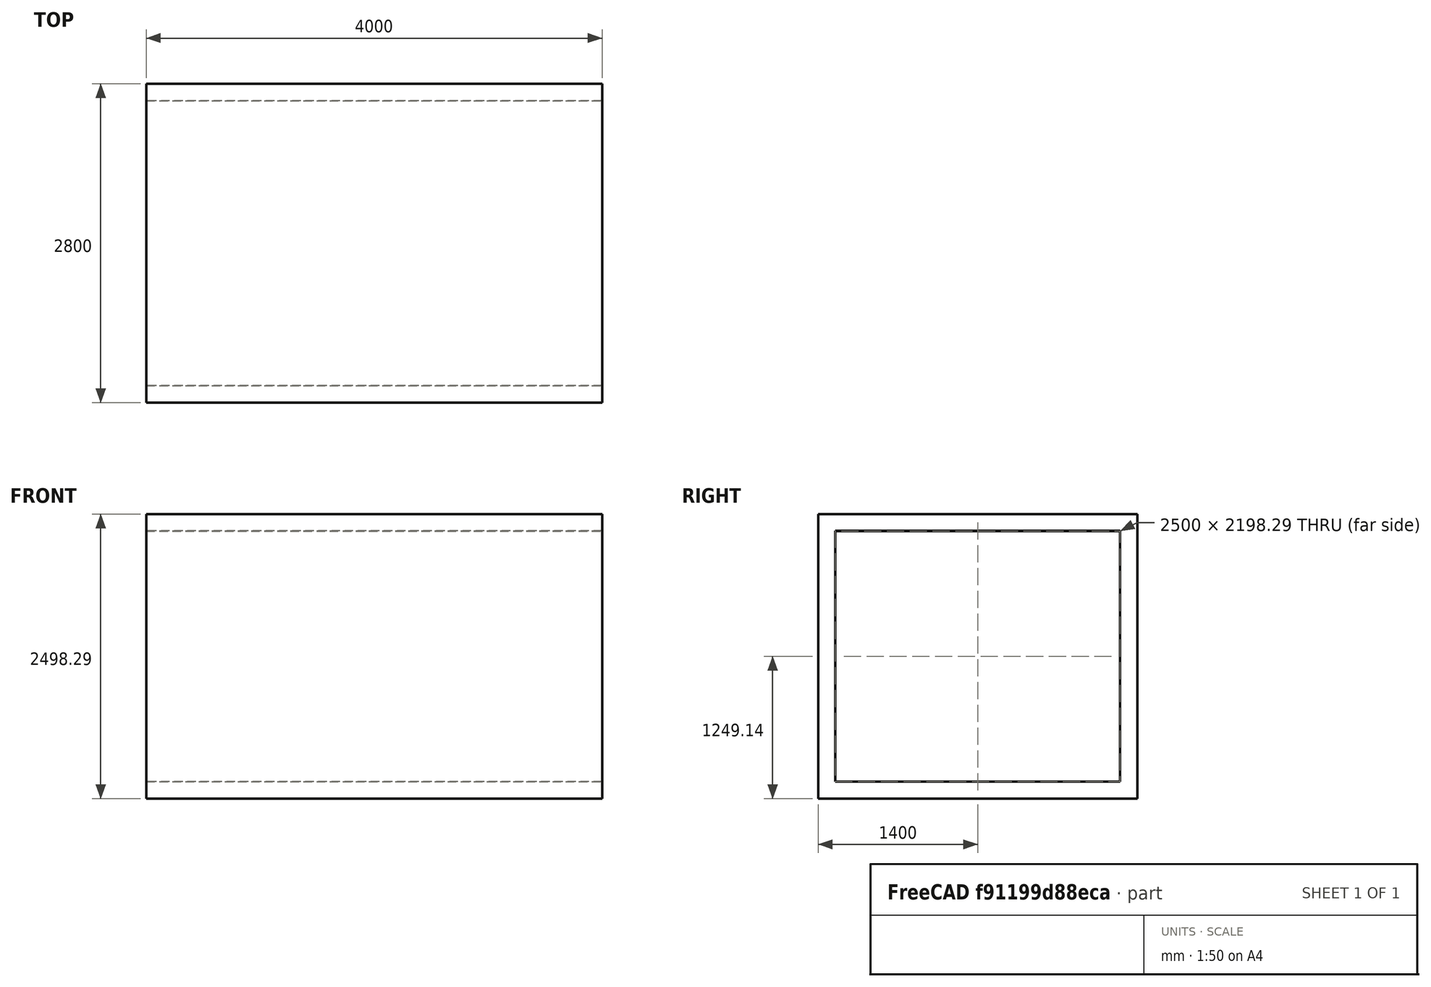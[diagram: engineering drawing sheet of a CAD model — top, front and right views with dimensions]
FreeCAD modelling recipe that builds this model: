
FCSTD DOCUMENT  (FreeCAD 0.17R10276 (Git))
Label: Base Quick Fit Plans 01
License: All rights reserved
LicenseURL: http://en.wikipedia.org/wiki/All_rights_reserved
objects: Part::Feature×204, Part::Part2DObjectPython×170, Part::Mirroring×20, App::DocumentObjectGroup×13, Part::Compound×9, App::FeaturePython×6, App::Annotation×2, Part::Extrusion×2, Part::FeaturePython×2, Part::Thickness×1, Sketcher::SketchObject×1
note: 409 computed .brp shape members not serialized (recipe doc carries the construction recipe); baked Part::Feature solids carry a one-line shape summary decoded from their .brp

FEATURE [Part::Part2DObjectPython] Rectangle  # Draft 2D object (typed FeaturePython)
  ChamferSize = 0
  Columns = 1
  FilletRadius = 0
  Height = 7500
  Length = 6000
  MakeFace = false
  MapMode = -1
  Placement = pos=(-92,-160,0) rot=(0,0,1;0rad)
  Rows = 1
FEATURE [App::FeaturePython] Dimension  # Draft dimension (typed FeaturePython)
  Diameter = false
  Dimline = (6612,4842,0)
  Direction = (0,0,0)
  Distance = 7500
  End = (5908,7340,0)
  LinkedGeometry = -> [Rectangle]
  Normal = (0,0,1)
  Start = (5908,-160,0)
  Support = -> Rectangle
FEATURE [App::FeaturePython] Dimension001  # Draft dimension (typed FeaturePython)
  Diameter = false
  Dimline = (3172,-852,0)
  Direction = (0,0,0)
  Distance = 6000
  End = (5908,-160,0)
  LinkedGeometry = -> [Rectangle]
  Normal = (0,0,1)
  Start = (-92,-160,0)
  Support = -> Rectangle
FEATURE [Part::Part2DObjectPython] Rectangle001  # Draft 2D object (typed FeaturePython)
  ChamferSize = 0
  Columns = 1
  FilletRadius = 0
  Height = 9000
  Length = 5000
  MakeFace = false
  MapMode = -1
  Placement = pos=(9194.87,-160,0) rot=(0,0,1;0rad)
  Rows = 1
FEATURE [App::FeaturePython] Dimension002  # Draft dimension (typed FeaturePython)
  Diameter = false
  Dimline = (15053,4856,0)
  Direction = (0,0,0)
  Distance = 9000
  End = (14194.9,8840,0)
  LinkedGeometry = -> [Rectangle001]
  Normal = (0,0,1)
  Start = (14194.9,-160,0)
  Support = -> Rectangle001
FEATURE [App::FeaturePython] Dimension003  # Draft dimension (typed FeaturePython)
  Diameter = false
  Dimline = (12458.9,-852,0)
  Direction = (0,0,0)
  Distance = 5000
  End = (14194.9,-160,0)
  LinkedGeometry = -> [Rectangle001]
  Normal = (0,0,1)
  Start = (9194.87,-160,0)
  Support = -> Rectangle001
FEATURE [Part::Part2DObjectPython] Rectangle002  # Draft 2D object (typed FeaturePython)
  ChamferSize = 0
  Columns = 1
  FilletRadius = 0
  Height = 11250
  Length = 4000
  MakeFace = false
  MapMode = -1
  Placement = pos=(17670.3,-160,0) rot=(0,0,1;0rad)
  Rows = 1
FEATURE [App::FeaturePython] Dimension004  # Draft dimension (typed FeaturePython)
  Diameter = false
  Dimline = (22786,4857,0)
  Direction = (0,0,0)
  Distance = 11250
  End = (21670.3,11090,0)
  LinkedGeometry = -> [Rectangle002]
  Normal = (0,0,1)
  Start = (21670.3,-160,0)
  Support = -> Rectangle002
FEATURE [App::FeaturePython] Dimension005  # Draft dimension (typed FeaturePython)
  Diameter = false
  Dimline = (20934.3,-852,0)
  Direction = (0,0,0)
  Distance = 4000
  End = (21670.3,-160,0)
  LinkedGeometry = -> [Rectangle002]
  Normal = (0,0,1)
  Start = (17670.3,-160,0)
  Support = -> Rectangle002
FEATURE [Part::Part2DObjectPython] Rectangle011  # Draft 2D object (typed FeaturePython)
  ChamferSize = 0
  Columns = 1
  FilletRadius = 0
  Height = 18
  Length = 900
  MakeFace = true
  Placement = pos=(3354.54,473.858,0) rot=(0.707107,0.707107,0;3.14159rad)
  Rows = 1
FEATURE [Part::Part2DObjectPython] Arc001  # Draft 2D object (typed FeaturePython)
  FirstAngle = -90
  LastAngle = 0
  MakeFace = true
  Placement = pos=(3372.54,473.858,0) rot=(0.707107,0.707107,0;3.14159rad)
  Radius = 900
FEATURE [Part::Part2DObjectPython] Rectangle012  # Draft 2D object (typed FeaturePython)
  ChamferSize = 0
  Columns = 1
  FilletRadius = 0
  Height = 18
  Length = 100
  MakeFace = true
  Placement = pos=(3390.54,373.858,0) rot=(0.707107,0.707107,0;3.14159rad)
  Rows = 1
FEATURE [Part::Part2DObjectPython] Rectangle013  # Draft 2D object (typed FeaturePython)
  ChamferSize = 0
  Columns = 1
  FilletRadius = 0
  Height = 18
  Length = 100
  MakeFace = true
  Placement = pos=(3372.54,373.858,0) rot=(0.707107,0.707107,0;3.14159rad)
  Rows = 1
FEATURE [Part::Part2DObjectPython] Rectangle014  # Draft 2D object (typed FeaturePython)
  ChamferSize = 0
  Columns = 1
  FilletRadius = 0
  Height = 18
  Length = 100
  MakeFace = true
  Placement = pos=(2436.54,373.858,0) rot=(0.707107,0.707107,0;3.14159rad)
  Rows = 1
FEATURE [Part::Part2DObjectPython] Rectangle015  # Draft 2D object (typed FeaturePython)
  ChamferSize = 0
  Columns = 1
  FilletRadius = 0
  Height = 18
  Length = 100
  MakeFace = true
  Placement = pos=(2454.54,373.858,0) rot=(0.707107,0.707107,0;3.14159rad)
  Rows = 1
FEATURE [Part::Compound] Compound001  label="Door-90cm"
  Links = -> [Rectangle015,Rectangle014,Rectangle011,Rectangle012,Arc001,Rectangle013]
  Placement = pos=(12065.1,-4816.3,0) rot=(0,0,1;0rad)
FEATURE [Part::Part2DObjectPython] Rectangle016  # Draft 2D object (typed FeaturePython)
  ChamferSize = 0
  Columns = 1
  FilletRadius = 0
  Height = 1450
  Length = 2250
  MakeFace = false
  Placement = pos=(19234,-3969.83,0) rot=(0.707107,0.707107,0;3.14159rad)
  Rows = 1
FEATURE [Part::Part2DObjectPython] Rectangle017  # Draft 2D object (typed FeaturePython)
  ChamferSize = 0
  Columns = 1
  FilletRadius = 0
  Height = 18
  Length = 800
  MakeFace = true
  Placement = pos=(4414.52,473.858,0) rot=(0.707107,0.707107,0;3.14159rad)
  Rows = 1
FEATURE [Part::Part2DObjectPython] Rectangle018  # Draft 2D object (typed FeaturePython)
  ChamferSize = 0
  Columns = 1
  FilletRadius = 0
  Height = 18
  Length = 100
  MakeFace = true
  Placement = pos=(4450.52,373.858,0) rot=(0.707107,0.707107,0;3.14159rad)
  Rows = 1
FEATURE [Part::Part2DObjectPython] Rectangle019  # Draft 2D object (typed FeaturePython)
  ChamferSize = 0
  Columns = 1
  FilletRadius = 0
  Height = 18
  Length = 100
  MakeFace = true
  Placement = pos=(4432.52,373.858,0) rot=(0.707107,0.707107,0;3.14159rad)
  Rows = 1
FEATURE [Part::Part2DObjectPython] Rectangle020  # Draft 2D object (typed FeaturePython)
  ChamferSize = 0
  Columns = 1
  FilletRadius = 0
  Height = 18
  Length = 100
  MakeFace = true
  Placement = pos=(3596.52,373.858,0) rot=(0.707107,0.707107,0;3.14159rad)
  Rows = 1
FEATURE [Part::Part2DObjectPython] Rectangle021  # Draft 2D object (typed FeaturePython)
  ChamferSize = 0
  Columns = 1
  FilletRadius = 0
  Height = 18
  Length = 100
  MakeFace = true
  Placement = pos=(3614.52,373.858,0) rot=(0.707107,0.707107,0;3.14159rad)
  Rows = 1
FEATURE [Part::Part2DObjectPython] Rectangle022  # Draft 2D object (typed FeaturePython)
  ChamferSize = 0
  Columns = 1
  FilletRadius = 0
  Height = 1655.27
  Length = 2455.27
  MakeFace = false
  Placement = pos=(19131.4,-4072.46,0) rot=(0.707107,0.707107,0;3.14159rad)
  Rows = 1
FEATURE [Part::Part2DObjectPython] Rectangle023  # Draft 2D object (typed FeaturePython)
  ChamferSize = 0
  Columns = 1
  FilletRadius = 0
  Height = 800
  Length = 800
  MakeFace = true
  Placement = pos=(21405.4,-1242.94,0) rot=(0.707107,0.707107,0;3.14159rad)
  Rows = 1
FEATURE [Part::Part2DObjectPython] Rectangle024  # Draft 2D object (typed FeaturePython)
  ChamferSize = 0
  Columns = 1
  FilletRadius = 0
  Height = 760
  Length = 760
  MakeFace = true
  Placement = pos=(21425.4,-1222.94,0) rot=(0.707107,0.707107,0;3.14159rad)
  Rows = 1
FEATURE [Part::Feature] Face
  Placement = pos=(15980.4,-1398.57,0) rot=(0,0,1;0rad)
  shape: bbox 800 x 800 x 2e-07 mm, 1 faces, 0 solids (baked)
FEATURE [Part::Part2DObjectPython] Rectangle025  # Draft 2D object (typed FeaturePython)
  ChamferSize = 0
  Columns = 1
  FilletRadius = 0
  Height = 760
  Length = 760
  MakeFace = true
  Placement = pos=(21425.4,-1222.94,0) rot=(0.707107,0.707107,0;3.14159rad)
  Rows = 1
FEATURE [Part::Part2DObjectPython] Line001  # Draft 2D object (typed FeaturePython)
  ChamferSize = 0
  Closed = false
  End = (21425.4,-1222.94,0)
  FilletRadius = 0
  Length = 1074.8
  MakeFace = true
  Placement = pos=(15980.4,-1398.57,0) rot=(0,0,1;0rad)
  Points = (2) [(6204.98,935.631,0),(5444.98,175.631,0)]
  Start = (22185.4,-462.938,0)
  Subdivisions = 0
FEATURE [Part::Part2DObjectPython] Line002  # Draft 2D object (typed FeaturePython)
  ChamferSize = 0
  Closed = false
  End = (22185.4,-1222.94,0)
  FilletRadius = 0
  Length = 1074.8
  MakeFace = true
  Placement = pos=(15980.4,-1398.57,0) rot=(0,0,1;0rad)
  Points = (2) [(5444.98,935.631,0),(6204.98,175.631,0)]
  Start = (21425.4,-462.938,0)
  Subdivisions = 0
FEATURE [Part::Part2DObjectPython] Block  label="Shower"  # Draft 2D object (typed FeaturePython)
  Components = -> [Line002,Line001,Rectangle025,Face]
  Placement = pos=(-1521.4,-1276.89,0) rot=(0,0,1;0rad)
FEATURE [Part::Part2DObjectPython] Rectangle026  # Draft 2D object (typed FeaturePython)
  ChamferSize = 0
  Columns = 1
  FilletRadius = 30
  Height = 370
  Length = 170
  MakeFace = true
  Placement = pos=(22375.3,-1817.54,0) rot=(0.707107,0.707107,0;3.14159rad)
  Rows = 1
FEATURE [Part::Part2DObjectPython] Circle  # Draft 2D object (typed FeaturePython)
  FirstAngle = 0
  LastAngle = 0
  MakeFace = true
  Placement = pos=(22560.3,-1732.54,0) rot=(0.707107,0.707107,0;3.14159rad)
  Radius = 10
  Support = -> [Rectangle026]
FEATURE [Part::Feature] Compound003  label="WC001"
  Placement = pos=(12977.9,-1470.8,0) rot=(0,0,1;0rad)
  shape: bbox 370 x 660 x 2e-07 mm, 2 faces, 0 solids (baked)
FEATURE [Part::Part2DObjectPython] Rectangle027  # Draft 2D object (typed FeaturePython)
  ChamferSize = 0
  Columns = 1
  FilletRadius = 50
  Height = 300
  Length = 500
  MakeFace = true
  Placement = pos=(21444.9,-2450.78,0) rot=(0.707107,0.707107,0;3.14159rad)
  Rows = 1
FEATURE [Part::Part2DObjectPython] Circle001  # Draft 2D object (typed FeaturePython)
  FirstAngle = 0
  LastAngle = 0
  MakeFace = true
  Placement = pos=(5532.19,-802.214,0) rot=(0,0,1;0rad)
  Radius = 12
FEATURE [Part::Feature] Face003
  shape: bbox 278.9 x 478.9 x 2e-07 mm, 1 faces, 0 solids (baked)
FEATURE [Part::Feature] Face004
  Placement = pos=(15980.4,-1398.57,0) rot=(0,0,1;0rad)
  shape: bbox 278.9 x 478.9 x 2e-07 mm, 1 faces, 0 solids (baked)
FEATURE [Part::Feature] Face005
  shape: bbox 300 x 500 x 2e-07 mm, 1 faces, 0 solids (baked)
FEATURE [Part::Compound] Compound004  label="Sink 1"
  Links = -> [Face005,Face003,Circle001]
  Placement = pos=(13769.5,-2367.61,0) rot=(0,0,1;0rad)
FEATURE [Part::Feature] Compound005  label="Sink"
  Placement = pos=(18979.2,3570.08,0) rot=(0,0,-1;1.5708rad)
  shape: bbox 500 x 300 x 2e-07 mm, 3 faces, 0 solids (baked)
FEATURE [Part::Feature] Compound006  label="WC002"
  Placement = pos=(12181.7,-1602.71,0) rot=(0,0,1;0rad)
  shape: bbox 370 x 660 x 2e-07 mm, 2 faces, 0 solids (baked)
FEATURE [Part::Part2DObjectPython] Arc002  # Draft 2D object (typed FeaturePython)
  FirstAngle = -90
  LastAngle = 0
  MakeFace = true
  Placement = pos=(4432.52,473.858,0) rot=(0.707107,0.707107,0;3.14159rad)
  Radius = 800
FEATURE [Part::Compound] Compound007  label="Door-80cm"
  Links = -> [Rectangle019,Rectangle017,Rectangle018,Rectangle020,Rectangle021,Arc002]
  Placement = pos=(12065.1,-4816.3,0) rot=(0,0,1;0rad)
FEATURE [Part::Part2DObjectPython] Rectangle028  # Draft 2D object (typed FeaturePython)
  ChamferSize = 0
  Columns = 1
  FilletRadius = 0
  Height = 400
  Length = 400
  MakeFace = true
  Placement = pos=(17670.3,-160,0) rot=(0.707107,0.707107,0;3.14159rad)
  Rows = 1
  Support = -> [Rectangle002]
FEATURE [Part::Feature] mirror008  label="Mirror of 90cm door001"
  Placement = pos=(3560.22,2517.25,0) rot=(0,0,1;0rad)
  shape: bbox 972 x 1000 x 2e-07 mm, 5 faces, 0 solids (baked)
FEATURE [Part::Feature] Compound010  label="90cm door003"
  Placement = pos=(22653.3,641.465,0) rot=(0,0,1;0rad)
  shape: bbox 972 x 1000 x 2e-07 mm, 5 faces, 0 solids (baked)
FEATURE [Part::Part2DObjectPython] Line003  # Draft 2D object (typed FeaturePython)
  ChamferSize = 0
  Closed = false
  End = (23811.8,1115.32,0)
  FilletRadius = 0
  Length = 1314
  MakeFace = true
  Placement = pos=(4391.51,-222,0) rot=(0,0,1;0rad)
  Points = (2) [(20734.3,1337.32,0),(19420.3,1337.32,0)]
  Start = (25125.8,1115.32,0)
  Subdivisions = 0
FEATURE [Part::Part2DObjectPython] Line  # Draft 2D object (typed FeaturePython)
  ChamferSize = 0
  Closed = false
  End = (26367.1,1115.32,0)
  FilletRadius = 0
  Length = 2499.64
  MakeFace = true
  Placement = pos=(4497.18,0,0) rot=(0,0,1;0rad)
  Points = (2) [(19370.3,1115.32,0),(21870,1115.32,0)]
  Start = (23867.5,1115.32,0)
  Subdivisions = 0
FEATURE [Part::Part2DObjectPython] Line005  # Draft 2D object (typed FeaturePython)
  ChamferSize = 0
  Closed = false
  End = (26261.5,960.561,0)
  FilletRadius = 0
  Length = 2499.64
  MakeFace = true
  Placement = pos=(4391.51,0,0) rot=(0,0,1;0rad)
  Points = (2) [(19370.3,960.561,0),(21870,960.561,0)]
  Start = (23761.8,960.561,0)
  Subdivisions = 0
FEATURE [App::DocumentObjectGroup] Construction
  Group = -> [Compound010,Line003,Line,Line005]
FEATURE [Part::Part2DObjectPython] Rectangle049  # Draft 2D object (typed FeaturePython)
  ChamferSize = 0
  Columns = 1
  FilletRadius = 0
  Height = 1900
  Length = 1400
  MakeFace = true
  Placement = pos=(-5091.08,-778.605,0) rot=(0,0,1;0rad)
  Rows = 1
FEATURE [Part::Part2DObjectPython] Rectangle050  # Draft 2D object (typed FeaturePython)
  ChamferSize = 0
  Columns = 1
  FilletRadius = 0
  Height = 1900
  Length = 910
  MakeFace = true
  Placement = pos=(-6241.3,-778.605,0) rot=(0,0,1;0rad)
  Rows = 1
FEATURE [Part::Part2DObjectPython] Rectangle051  # Draft 2D object (typed FeaturePython)
  ChamferSize = 0
  Columns = 1
  FilletRadius = 0
  Height = 300
  Length = 910
  MakeFace = true
  Placement = pos=(-6241.3,821.395,0) rot=(0,0,1;0rad)
  Rows = 1
FEATURE [Part::Part2DObjectPython] Line008  # Draft 2D object (typed FeaturePython)
  ChamferSize = 0
  Closed = false
  End = (-5786.3,821.395,0)
  FilletRadius = 0
  Length = 647.012
  MakeFace = true
  Points = (2) [(-6241.3,361.395,0),(-5786.3,821.395,0)]
  Start = (-6241.3,361.395,0)
  Subdivisions = 0
FEATURE [Part::Part2DObjectPython] DWire001  # Draft 2D object (typed FeaturePython)
  ChamferSize = 0
  Closed = true
  End = (-6241.3,361.395,0)
  FilletRadius = 0
  Length = 1562.01
  MakeFace = true
  Points = (3) [(-5786.3,821.395,0),(-5786.3,361.395,0),(-6241.3,361.395,0)]
  Start = (-5786.3,821.395,0)
  Subdivisions = 0
FEATURE [Part::Part2DObjectPython] DWire002  # Draft 2D object (typed FeaturePython)
  ChamferSize = 0
  Closed = true
  End = (-5091.08,361.395,0)
  FilletRadius = 0
  Length = 1562.01
  MakeFace = true
  Placement = pos=(1150.22,0,0) rot=(0,0,1;0rad)
  Points = (3) [(-5786.3,821.395,0),(-5786.3,361.395,0),(-6241.3,361.395,0)]
  Start = (-4636.08,821.395,0)
  Subdivisions = 0
FEATURE [Part::Part2DObjectPython] Rectangle052  # Draft 2D object (typed FeaturePython)
  ChamferSize = 0
  Columns = 1
  FilletRadius = 0
  Height = 300
  Length = 700
  MakeFace = true
  Placement = pos=(-5091.08,821.395,0) rot=(0,0,1;0rad)
  Rows = 1
FEATURE [Part::Part2DObjectPython] Rectangle053  # Draft 2D object (typed FeaturePython)
  ChamferSize = 0
  Columns = 1
  FilletRadius = 0
  Height = 300
  Length = 700
  MakeFace = true
  Placement = pos=(-4391.08,821.395,0) rot=(0,0,1;0rad)
  Rows = 1
FEATURE [Part::Compound] Compound009  label="Bed-Twin"
  Links = -> [Rectangle050,Rectangle051,Line008,DWire001]
FEATURE [App::DocumentObjectGroup] Group003  label="Assets"
  Group = -> [Compound005,Compound006,Compound001,Compound007,Compound009]
FEATURE [Part::Part2DObjectPython] DWire005  # Draft 2D object (typed FeaturePython)
  ChamferSize = 0
  Closed = true
  End = (-3474.44,-2441.09,0)
  FilletRadius = 0
  Length = 5366.71
  MakeFace = true
  Points = (8) [(-3691.08,-2441.09,0),(-3691.08,-1691.09,0),(-2291.08,-1691.09,0),(-2291.08,-2441.09,0),(-2507.72,-2441.09,0),(-2507.72,-1907.73,0),+2 more]
  Start = (-3691.08,-2441.09,0)
  Subdivisions = 0
FEATURE [Part::Part2DObjectPython] Rectangle035  # Draft 2D object (typed FeaturePython)
  ChamferSize = 0
  Columns = 1
  FilletRadius = 0
  Height = 533.356
  Length = 966.713
  MakeFace = true
  Placement = pos=(-3474.44,-2441.09,0) rot=(0,0,1;0rad)
  Rows = 1
FEATURE [Part::Part2DObjectPython] Line012  # Draft 2D object (typed FeaturePython)
  ChamferSize = 0
  Closed = false
  End = (-2991.08,-2441.09,0)
  FilletRadius = 0
  Length = 533.356
  MakeFace = true
  Points = (2) [(-2991.08,-1907.73,0),(-2991.08,-2441.09,0)]
  Start = (-2991.08,-1907.73,0)
  Subdivisions = 0
FEATURE [Part::Part2DObjectPython] Line004  # Draft 2D object (typed FeaturePython)
  ChamferSize = 0
  Closed = false
  End = (-947.957,-2441.09,0)
  FilletRadius = 0
  Length = 533.356
  MakeFace = true
  Placement = pos=(2043.12,0,0) rot=(0,0,1;0rad)
  Points = (2) [(-2991.08,-1907.73,0),(-2991.08,-2441.09,0)]
  Start = (-947.957,-1907.73,0)
  Subdivisions = 0
FEATURE [Part::Part2DObjectPython] DWire006  # Draft 2D object (typed FeaturePython)
  ChamferSize = 0
  Closed = true
  End = (-1431.31,-2441.09,0)
  FilletRadius = 0
  Length = 6333.43
  MakeFace = true
  Placement = pos=(2043.12,0,0) rot=(0,0,1;0rad)
  Points = (8) [(-3691.08,-2441.09,0),(-3691.08,-1691.09,0),(-1807.72,-1691.09,0),(-1807.72,-2441.09,0),(-2024.37,-2441.09,0),(-2024.37,-1907.73,0),+2 more]
  Start = (-1647.96,-2441.09,0)
  Subdivisions = 0
FEATURE [Part::Part2DObjectPython] DWire007  # Draft 2D object (typed FeaturePython)
  ChamferSize = 0
  Closed = true
  End = (-5457.85,-2441.09,0)
  FilletRadius = 0
  Length = 4400
  MakeFace = true
  Placement = pos=(-1983.42,0,0) rot=(0,0,1;0rad)
  Points = (8) [(-3691.08,-2441.09,0),(-3691.08,-1691.09,0),(-2774.44,-1691.09,0),(-2774.44,-2441.09,0),(-2991.08,-2441.09,0),(-2991.08,-1907.73,0),+2 more]
  Start = (-5674.49,-2441.09,0)
  Subdivisions = 0
FEATURE [Part::Part2DObjectPython] Rectangle037  # Draft 2D object (typed FeaturePython)
  ChamferSize = 0
  Columns = 1
  FilletRadius = 0
  Height = 533.356
  Length = 483.356
  MakeFace = true
  Placement = pos=(-5457.85,-2441.09,0) rot=(0,0,1;0rad)
  Rows = 1
FEATURE [Part::Compound] Compound021  label="Sofa - 1"
  Links = -> [DWire005,Rectangle035,Line012]
FEATURE [Part::Compound] Compound011  label="Sofa - 2"
  Links = -> [Rectangle037,DWire007]
FEATURE [Part::Part2DObjectPython] Rectangle038  # Draft 2D object (typed FeaturePython)
  ChamferSize = 0
  Columns = 1
  FilletRadius = 0
  Height = 533.356
  Length = 1450.07
  MakeFace = true
  Placement = pos=(-1431.31,-2441.09,0) rot=(0,0,1;0rad)
  Rows = 1
FEATURE [Part::Part2DObjectPython] Line006  # Draft 2D object (typed FeaturePython)
  ChamferSize = 0
  Closed = false
  End = (-464.6,-2441.09,0)
  FilletRadius = 0
  Length = 533.356
  MakeFace = true
  Placement = pos=(2526.48,0,0) rot=(0,0,1;0rad)
  Points = (2) [(-2991.08,-1907.73,0),(-2991.08,-2441.09,0)]
  Start = (-464.6,-1907.73,0)
  Subdivisions = 0
FEATURE [Part::Compound] Compound022  label="Sofa - 3"
  Links = -> [Line004,DWire006,Rectangle038,Line006]
FEATURE [Part::Compound] Compound008  label="Bed-Double"
  Links = -> [Rectangle049,DWire002,Rectangle052,Rectangle053]
FEATURE [Part::Feature] Compound024  label="90cm door005"
  Placement = pos=(26285.8,79.011,0) rot=(0,0,1;1.5708rad)
  shape: bbox 1000 x 972 x 2e-07 mm, 5 faces, 0 solids (baked)
FEATURE [Part::Part2DObjectPython] Rectangle054  # Draft 2D object (typed FeaturePython)
  ChamferSize = 0
  Columns = 1
  FilletRadius = 0
  Height = 600
  Length = 2923.45
  MakeFace = true
  Placement = pos=(18270.3,2237.32,0) rot=(0,0,1;1.5708rad)
  Rows = 1
FEATURE [Part::Mirroring] mirror009  label="Mirror of Sink"
  Base = (18377,-1894.45,0)
  Normal = (0,1,0)
  Source = -> Compound005
FEATURE [Part::Feature] mirror010  label="Mirror of Sink001"
  Placement = pos=(19714.8,21927.3,0) rot=(0,0,-1;1.5708rad)
  shape: bbox 300 x 500 x 2e-07 mm, 3 faces, 0 solids (baked)
FEATURE [Part::Feature] Shell002  label="Dinning 002"
  Placement = pos=(-2420.47,1941.18,0) rot=(0,0,1;0rad)
  shape: bbox 2057 x 2057 x 2e-07 mm, 5 faces, 0 solids (baked)
FEATURE [Part::Feature] Shell003  label="Dinning 003"
  Placement = pos=(-7725.86,-2470.88,0) rot=(0,0,1;0rad)
  shape: bbox 2057 x 2057 x 2e-07 mm, 5 faces, 0 solids (baked)
FEATURE [Part::Feature] Compound027  label="dinning001"
  Placement = pos=(-14334.8,-3411.08,0) rot=(0,0,1;0rad)
  shape: bbox 2057 x 1200 x 2e-07 mm, 5 faces, 0 solids (baked)
FEATURE [Part::Feature] Compound029  label="Door-90cm002"
  Placement = pos=(4421.79,-3083.36,0) rot=(0,0,1;0rad)
  shape: bbox 972 x 1000 x 2e-07 mm, 5 faces, 0 solids (baked)
FEATURE [Part::Feature] Compound030  label="Bed-Double003"
  Placement = pos=(9599.08,5590.61,0) rot=(0,0,1;0rad)
  shape: bbox 1400 x 1900 x 2e-07 mm, 4 faces, 0 solids (baked)
FEATURE [Part::Feature] mirror013  label="Mirror of Shower002"
  Placement = pos=(-9357.23,5973.34,0) rot=(0,0,1;0rad)
  shape: bbox 800 x 800 x 2e-07 mm, 2 faces, 0 solids (baked)
FEATURE [Part::Feature] mirror017  label="Mirror of Sofa - 006"
  Placement = pos=(5211.98,2057.23,0) rot=(0,0,1;0rad)
  shape: bbox 1400 x 750 x 2e-07 mm, 2 faces, 0 solids (baked)
FEATURE [Part::Feature] Compound031  label="Sofa - 006"
  Placement = pos=(27672.7,9569.4,0) rot=(0,0,1;0rad)
  shape: bbox 1400 x 750 x 2e-07 mm, 2 faces, 0 solids (baked)
FEATURE [Part::Feature] Compound034  label="Bed-Double004"
  Placement = pos=(15177.5,-4723.55,0) rot=(0,0,1;0rad)
  shape: bbox 1400 x 1900 x 2e-07 mm, 4 faces, 0 solids (baked)
FEATURE [Part::Feature] Compound035  label="Bed-Double005"
  Placement = pos=(12639.4,2140.46,0) rot=(0,0,1;1.5708rad)
  shape: bbox 1900 x 1400 x 2e-07 mm, 4 faces, 0 solids (baked)
FEATURE [Part::Part2DObjectPython] Rectangle070  # Draft 2D object (typed FeaturePython)
  ChamferSize = 0
  Columns = 1
  FilletRadius = 0
  Height = 3000
  Length = 3000
  MakeFace = true
  Placement = pos=(6000,-9774.06,0) rot=(0,0,1;0rad)
  Rows = 1
FEATURE [Part::Part2DObjectPython] Rectangle072  # Draft 2D object (typed FeaturePython)
  ChamferSize = 0
  Columns = 1
  FilletRadius = 0
  Height = 600
  Length = 3599.13
  MakeFace = true
  Placement = pos=(2308.87,8523.32,0) rot=(0,0,1;0rad)
  Rows = 1
FEATURE [Part::Feature] mirror030  label="Mirror of Sink 005"
  Placement = pos=(4044.83,28204.3,0) rot=(0,0,-1;1.5708rad)
  shape: bbox 500 x 300 x 2e-07 mm, 3 faces, 0 solids (baked)
FEATURE [Part::Part2DObjectPython] Rectangle073  # Draft 2D object (typed FeaturePython)
  ChamferSize = 0
  Columns = 1
  FilletRadius = 0
  Height = 1950
  Length = 950
  MakeFace = true
  Placement = pos=(1798.43,-5839.95,0) rot=(0,0,1;0rad)
  Rows = 1
FEATURE [App::DocumentObjectGroup] Group006  label="Plan Layout 2"
  Group = -> [Compound035,Rectangle070,Rectangle073]
FEATURE [App::DocumentObjectGroup] Group001  label="9mx5m"
  Group = -> [Dimension002,Dimension003,Rectangle001,Group006]
FEATURE [Part::Feature] Compound048
  Placement = pos=(2515.93,6885.08,0) rot=(0,0,-1;1.5708rad)
  shape: bbox 1950 x 2057 x 2e-07 mm, 7 faces, 0 solids (baked)
FEATURE [Part::Feature] Compound049
  Placement = pos=(-6428.78,862.396,0) rot=(0,0,1;0rad)
  shape: bbox 2057 x 1950 x 2e-07 mm, 7 faces, 0 solids (baked)
FEATURE [Part::Part2DObjectPython] Line016  # Draft 2D object (typed FeaturePython)
  ChamferSize = 0
  Closed = false
  End = (5908,8823.32,0)
  FilletRadius = 0
  Length = 3599.13
  MakeFace = true
  Placement = pos=(0,1783.32,0) rot=(0,0,1;0rad)
  Points = (2) [(2308.87,7040,0),(5908,7040,0)]
  Start = (2308.87,8823.32,0)
  Subdivisions = 0
FEATURE [Part::Part2DObjectPython] Rectangle075  # Draft 2D object (typed FeaturePython)
  ChamferSize = 0
  Columns = 1
  FilletRadius = 0
  Height = 600
  Length = 150.814
  MakeFace = false
  Placement = pos=(3257.19,2489.19,0) rot=(0,0,1;0rad)
  Rows = 1
FEATURE [Part::Part2DObjectPython] Rectangle078  # Draft 2D object (typed FeaturePython)
  ChamferSize = 0
  Columns = 1
  FilletRadius = 0
  Height = 2500
  Length = 4000
  MakeFace = false
  Placement = pos=(17670.3,8590,0) rot=(0,0,1;0rad)
  Rows = 1
FEATURE [Part::Part2DObjectPython] Rectangle079  # Draft 2D object (typed FeaturePython)
  ChamferSize = 0
  Columns = 1
  FilletRadius = 0
  Height = 7500
  Length = 3752.68
  MakeFace = false
  Placement = pos=(2155.32,-160,0) rot=(0,0,1;0rad)
  Rows = 7
FEATURE [App::Annotation] Text
  LabelText = Single Bed Unit 45 sq m | 1 Bed | Bath | Kitchen | Living
  Position = (-173.725,11590.6,0)
FEATURE [Part::Part2DObjectPython] Line017  # Draft 2D object (typed FeaturePython)
  ChamferSize = 0
  Closed = false
  End = (19420.3,11090,0)
  FilletRadius = 0
  Length = 8852.68
  MakeFace = true
  Points = (2) [(19420.3,2237.32,0),(19420.3,11090,0)]
  Start = (19420.3,2237.32,0)
  Subdivisions = 0
FEATURE [Part::Feature] Compound012  label="Bed-Double002"
  Placement = pos=(18791.7,14231.1,0) rot=(0,0,1;1.5708rad)
  shape: bbox 1900 x 1400 x 2e-07 mm, 4 faces, 0 solids (baked)
FEATURE [App::DocumentObjectGroup] Group005  label="Plan Layout 3"
  Group = -> [Rectangle054,Compound012,mirror017,Compound031,Compound024,mirror010]
FEATURE [App::DocumentObjectGroup] Group002  label="11.5mx4m"
  Group = -> [Dimension004,Dimension005,Rectangle002,Group005]
FEATURE [Part::Feature] Compound  label="Sofa - 007"
  Placement = pos=(19318.3,10129.4,0) rot=(0,0,1;0rad)
  shape: bbox 1883 x 750 x 2e-07 mm, 2 faces, 0 solids (baked)
FEATURE [Part::Part2DObjectPython] Rectangle082  # Draft 2D object (typed FeaturePython)
  ChamferSize = 0
  Columns = 1
  FilletRadius = 0
  Height = 2803.44
  Length = 4303.44
  MakeFace = false
  Placement = pos=(17518.6,8438.28,0) rot=(0,0,1;0rad)
  Rows = 1
FEATURE [App::DocumentObjectGroup] Group007  label="Info"
  Group = -> [Text]
FEATURE [Part::Part2DObjectPython] Rectangle083  # Draft 2D object (typed FeaturePython)
  ChamferSize = 0
  Columns = 1
  FilletRadius = 0
  Height = 950
  Length = 950
  MakeFace = true
  Placement = pos=(18152.7,6324.53,0) rot=(0.707107,0.707107,0;3.14159rad)
  Rows = 1
FEATURE [Part::Feature] mirror035  label="Mirror of Sofa - 016"
  shape: bbox 1883 x 750 x 2e-07 mm, 2 faces, 0 solids (baked)
FEATURE [Part::Part2DObjectPython] Line023  # Draft 2D object (typed FeaturePython)
  ChamferSize = 0
  Closed = false
  End = (21670.3,5160.77,0)
  FilletRadius = 0
  Length = 4000
  MakeFace = true
  Points = (2) [(17670.3,5160.77,0),(21670.3,5160.77,0)]
  Start = (17670.3,5160.77,0)
  Subdivisions = 0
FEATURE [Part::Feature] Compound051  label="dinning003"
  Placement = pos=(29919.6,-14497.4,0) rot=(0,0,1;1.5708rad)
  shape: bbox 1200 x 2057 x 2e-07 mm, 5 faces, 0 solids (baked)
FEATURE [Part::Part2DObjectPython] Rectangle090  # Draft 2D object (typed FeaturePython)
  ChamferSize = 0
  Columns = 1
  FilletRadius = 0
  Height = 3349.19
  Length = 150
  MakeFace = false
  Placement = pos=(-92,1289.19,0) rot=(0,0,-1;1.5708rad)
  Rows = 1
FEATURE [Part::Feature] mirror044  label="Mirror of Mirror of Shower002"
  Placement = pos=(-2698.48,-4e-12,0) rot=(0,0,1;0rad)
  shape: bbox 800 x 800 x 2e-07 mm, 2 faces, 0 solids (baked)
FEATURE [Part::Feature] mirror045  label="Mirror of Mirror of WC003"
  Placement = pos=(-2698.48,-4e-12,0) rot=(0,0,1;0rad)
  shape: bbox 370 x 660 x 2e-07 mm, 2 faces, 0 solids (baked)
FEATURE [Part::Feature] mirror046  label="Mirror of Rectangle090"
  Placement = pos=(-2698.48,-4e-12,0) rot=(0,0,1;0rad)
  shape: bbox 1900 x 2547 x 2e-07 mm, 0 faces, 0 solids (baked)
FEATURE [Part::Feature] mirror047  label="Mirror of Rectangle091"
  Placement = pos=(-2698.48,-4e-12,0) rot=(0,0,1;0rad)
  shape: bbox 1600 x 2247 x 2e-07 mm, 0 faces, 0 solids (baked)
FEATURE [Part::Feature] mirror048  label="Mirror of Mirror of Sink 007"
  Placement = pos=(-2698.48,-4e-12,0) rot=(0,0,1;0rad)
  shape: bbox 300 x 500 x 2e-07 mm, 3 faces, 0 solids (baked)
FEATURE [Part::Part2DObjectPython] Rectangle092  # Draft 2D object (typed FeaturePython)
  ChamferSize = 0
  Columns = 6
  FilletRadius = 0
  Height = 4000
  Length = 6502.68
  MakeFace = false
  Placement = pos=(17670.3,2087.32,0) rot=(0.707107,0.707107,0;3.14159rad)
  Rows = 1
FEATURE [Part::Feature] Compound052  label="Sofa - 008"
  Placement = pos=(1555.96,6630.22,0) rot=(0,0,1;0rad)
  shape: bbox 1883 x 750 x 2e-07 mm, 2 faces, 0 solids (baked)
FEATURE [Part::Part2DObjectPython] Rectangle093  # Draft 2D object (typed FeaturePython)
  ChamferSize = 0
  Columns = 1
  FilletRadius = 0
  Height = 950
  Length = 950
  MakeFace = true
  Placement = pos=(390.401,2825.38,0) rot=(0.707107,0.707107,0;3.14159rad)
  Rows = 1
FEATURE [Part::Feature] mirror052  label="Mirror of Sofa - 017"
  Placement = pos=(-17762.3,-3499.15,0) rot=(0,0,1;0rad)
  shape: bbox 1883 x 750 x 2e-07 mm, 2 faces, 0 solids (baked)
FEATURE [Part::Feature] mirror053  label="Mirror of Bed-Double005"
  Placement = pos=(-2125.14,1590.4,0) rot=(0,0,1;0rad)
  shape: bbox 1400 x 1900 x 2e-07 mm, 4 faces, 0 solids (baked)
FEATURE [Part::Part2DObjectPython] Rectangle094  # Draft 2D object (typed FeaturePython)
  ChamferSize = 0
  Columns = 18
  FilletRadius = 0
  Height = 2250
  Length = 2211.32
  MakeFace = false
  Placement = pos=(17670.3,-160,0) rot=(0.707107,0.707107,0;3.14159rad)
  Rows = 1
FEATURE [Part::Feature] Compound055  label="dinning004"
  Placement = pos=(-1210.3,-14381.2,0) rot=(0,0,1;1.5708rad)
  shape: bbox 1200 x 2057 x 2e-07 mm, 5 faces, 0 solids (baked)
FEATURE [Part::Feature] mirror062  label="Mirror of Compound059"
  Placement = pos=(4548.65,3195.2,0) rot=(0,0,1;0rad)
  shape: bbox 1907 x 2554 x 2e-07 mm, 7 faces, 0 solids (baked)
FEATURE [Part::Feature] mirror066  label="Mirror of Compound060"
  Placement = pos=(-1907.09,0,0) rot=(0,0,1;0rad)
  shape: bbox 1907 x 2554 x 2e-07 mm, 7 faces, 0 solids (baked)
FEATURE [Part::Part2DObjectPython] Rectangle102  # Draft 2D object (typed FeaturePython)
  ChamferSize = 0
  Columns = 1
  FilletRadius = 0
  Height = 1746.46
  Length = 1189.19
  MakeFace = true
  Placement = pos=(1661.54,6302.77,0) rot=(0.707107,0.707107,0;3.14159rad)
  Rows = 1
FEATURE [Part::Feature] mirror071  label="Mirror of Mirror of 90cm door010"
  Placement = pos=(-156.608,3268.49,0) rot=(0,0,1;0rad)
  shape: bbox 1000 x 972 x 2e-07 mm, 5 faces, 0 solids (baked)
FEATURE [Part::Feature] Compound058  label="90cm door006"
  Placement = pos=(8429.63,-2705.28,0) rot=(0,0,1;1.5708rad)
  shape: bbox 1000 x 972 x 2e-07 mm, 5 faces, 0 solids (baked)
FEATURE [Part::Feature] Compound061  label="Compound050"
  Placement = pos=(-951.5,6012.83,0) rot=(0,0,1;0rad)
  shape: bbox 2057 x 1950 x 2e-07 mm, 7 faces, 0 solids (baked)
FEATURE [Part::Mirroring] mirror084  label="Mirror of Door-90cm007"
  Base = (4121.31,-1938.87,0)
  Normal = (-1,0,0)
FEATURE [Part::Part2DObjectPython] Rectangle113  # Draft 2D object (typed FeaturePython)
  ChamferSize = 0
  Columns = 13
  FilletRadius = 0
  Height = 1595.64
  Length = 1037.23
  MakeFace = false
  Placement = pos=(1661.54,6302.77,0) rot=(0.707107,0.707107,0;3.14159rad)
  Rows = 1
FEATURE [Part::Feature] mirror088  label="Mirror of Mirror of Mirror of 90cm door007"
  Placement = pos=(-6324.81,751.517,0) rot=(0,0,1;0rad)
  shape: bbox 1000 x 972 x 2e-07 mm, 5 faces, 0 solids (baked)
FEATURE [Part::Feature] mirror090  label="Mirror of Mirror of 90cm door013"
  Placement = pos=(-23936.2,-2627.64,0) rot=(0,0,1;0rad)
  shape: bbox 1000 x 972 x 2e-07 mm, 5 faces, 0 solids (baked)
FEATURE [Part::Feature] mirror091  label="Mirror of 90cm door008"
  Placement = pos=(-35773.7,-3233,0) rot=(0,0,1;0rad)
  shape: bbox 1000 x 972 x 2e-07 mm, 5 faces, 0 solids (baked)
FEATURE [Part::Feature] mirror092  label="Mirror of Mirror of 90cm door014"
  Placement = pos=(-23936.2,-2627.64,0) rot=(0,0,1;0rad)
  shape: bbox 1000 x 972 x 2e-07 mm, 5 faces, 0 solids (baked)
FEATURE [Part::Feature] mirror094  label="Mirror of 90cm door009"
  Placement = pos=(-18703.5,21483.8,0) rot=(0,0,-1;1.5708rad)
  shape: bbox 972 x 1000 x 2e-07 mm, 5 faces, 0 solids (baked)
FEATURE [Part::Feature] mirror095  label="Mirror of Mirror of 90cm door016"
  Placement = pos=(-18098.2,9646.33,0) rot=(0,0,-1;1.5708rad)
  shape: bbox 972 x 1000 x 2e-07 mm, 5 faces, 0 solids (baked)
FEATURE [Part::Feature] mirror096  label="Mirror of Mirror of Mirror of 90cm door009"
  Placement = pos=(-18098.2,9646.33,0) rot=(0,0,-1;1.5708rad)
  shape: bbox 972 x 1000 x 2e-07 mm, 5 faces, 0 solids (baked)
FEATURE [App::Annotation] Text002
  LabelText = 90cm Door Bank 
  Position = (-17039.1,-18.7112,0)
FEATURE [Part::Part2DObjectPython] Rectangle114  # Draft 2D object (typed FeaturePython)
  ChamferSize = 0
  Columns = 1
  FilletRadius = 0
  Height = 1595.64
  Length = 146.163
  MakeFace = false
  Placement = pos=(1661.54,6302.77,0) rot=(0,0,-1;1.5708rad)
  Rows = 1
FEATURE [Part::Part2DObjectPython] Rectangle115  # Draft 2D object (typed FeaturePython)
  ChamferSize = 0
  Columns = 1
  FilletRadius = 0
  Height = 7802.78
  Length = 2801.63
  MakeFace = false
  Placement = pos=(3257.19,-310.814,0) rot=(0,0,1;0rad)
  Rows = 1
FEATURE [Part::Part2DObjectPython] Rectangle116  # Draft 2D object (typed FeaturePython)
  ChamferSize = 0
  Columns = 1
  FilletRadius = 0
  Height = 600
  Length = 2500
  MakeFace = true
  Placement = pos=(3408,3240,0) rot=(0,0,1;0rad)
  Rows = 1
FEATURE [Part::Part2DObjectPython] Rectangle117  # Draft 2D object (typed FeaturePython)
  ChamferSize = 0
  Columns = 1
  FilletRadius = 0
  Height = 3249.19
  Length = 2500
  MakeFace = true
  Placement = pos=(3408,-160,0) rot=(0,0,1;0rad)
  Rows = 1
FEATURE [Part::Part2DObjectPython] Rectangle119  # Draft 2D object (typed FeaturePython)
  ChamferSize = 0
  Columns = 1
  FilletRadius = 0
  Height = 4100
  Length = 2500
  MakeFace = true
  Placement = pos=(3408,3240,0) rot=(0,0,1;0rad)
  Rows = 1
FEATURE [Part::Part2DObjectPython] Rectangle120  # Draft 2D object (typed FeaturePython)
  ChamferSize = 0
  Columns = 1
  FilletRadius = 0
  Height = 4401.63
  Length = 2801.63
  MakeFace = true
  Placement = pos=(3257.19,3089.19,0) rot=(0,0,1;0rad)
  Rows = 1
FEATURE [Part::Part2DObjectPython] Rectangle121  # Draft 2D object (typed FeaturePython)
  ChamferSize = 0
  Columns = 1
  FilletRadius = 0
  Height = 3550.81
  Length = 2801.63
  MakeFace = true
  Placement = pos=(3257.19,-310.814,0) rot=(0,0,1;0rad)
  Rows = 1
FEATURE [Part::Feature] Compound064  label="Sofa - 010"
  Placement = pos=(-4732.17,-2088.69,0) rot=(0,0,1;1.5708rad)
  shape: bbox 750 x 1400 x 2e-07 mm, 2 faces, 0 solids (baked)
FEATURE [Part::Part2DObjectPython] Rectangle122  # Draft 2D object (typed FeaturePython)
  ChamferSize = 0
  Columns = 1
  FilletRadius = 0
  Height = 600
  Length = 2500
  MakeFace = true
  Placement = pos=(3408,2489.19,0) rot=(0,0,1;0rad)
  Rows = 1
FEATURE [Part::Part2DObjectPython] Line025  # Draft 2D object (typed FeaturePython)
  ChamferSize = 0
  Closed = false
  End = (5908,2789.19,0)
  FilletRadius = 0
  Length = 2500
  MakeFace = true
  Placement = pos=(549.567,-4250.81,0) rot=(0,0,1;0rad)
  Points = (2) [(2858.43,7040,0),(5358.43,7040,0)]
  Start = (3408,2789.19,0)
  Subdivisions = 0
FEATURE [Part::Feature] mirror104  label="Mirror of Sink 008"
  Placement = pos=(4722.56,22170.2,0) rot=(0,0,-1;1.5708rad)
  shape: bbox 500 x 300 x 2e-07 mm, 3 faces, 0 solids (baked)
FEATURE [Part::Part2DObjectPython] Rectangle125  # Draft 2D object (typed FeaturePython)
  ChamferSize = 0
  Columns = 1
  FilletRadius = 0
  Height = 2500
  Length = 600.001
  MakeFace = true
  Placement = pos=(21070.3,8590,0) rot=(0,0,1;0rad)
  Rows = 1
FEATURE [Part::Feature] Clone001  label="Clone of Door-90cm004"
  Placement = pos=(17661.8,8116.14,0) rot=(0,0,1;0rad)
  shape: bbox 972 x 1000 x 2e-07 mm, 5 faces, 0 solids (baked)
FEATURE [Part::Part2DObjectPython] Rectangle127  # Draft 2D object (typed FeaturePython)
  ChamferSize = 0
  Columns = 1
  FilletRadius = 0
  Height = 2015.84
  Length = 150.814
  MakeFace = false
  Placement = pos=(21070.3,6422.44,0) rot=(0,0,1;0rad)
  Rows = 1
FEATURE [Part::Part2DObjectPython] Rectangle128  # Draft 2D object (typed FeaturePython)
  ChamferSize = 0
  Columns = 1
  FilletRadius = 0
  Height = 4000
  Length = 2500
  MakeFace = true
  Placement = pos=(17670.3,8590,0) rot=(0.707107,0.707107,0;3.14159rad)
  Rows = 1
FEATURE [Part::Extrusion] Extrusion
  Base = -> Rectangle128
  Dir = (0,0,2198.29)
  DirMode = 0
  FaceMakerClass = Part::FaceMakerBullseye
  LengthFwd = 0
  LengthRev = 0
  Solid = true
  Symmetric = false
FEATURE [Part::Thickness] Thickness
  Faces = -> Extrusion [Face3,Face1]
  Intersection = false
  Join = 2
  Mode = 0
  SelfIntersection = false
  Value = 150
FEATURE [Part::Part2DObjectPython] Rectangle129  # Draft 2D object (typed FeaturePython)
  ChamferSize = 0
  Columns = 1
  FilletRadius = 0
  Height = 2500
  Length = 4000
  MakeFace = true
  Placement = pos=(17670.3,8590,0) rot=(0,0,1;0rad)
  Rows = 1
FEATURE [Part::Extrusion] Extrusion001
  Base = -> Rectangle129
  Dir = (0,0,2200)
  DirMode = 0
  FaceMakerClass = Part::FaceMakerBullseye
  LengthFwd = 0
  LengthRev = 0
  Solid = true
  Symmetric = false
FEATURE [Part::Part2DObjectPython] Line027  # Draft 2D object (typed FeaturePython)
  ChamferSize = 0
  Closed = false
  End = (17970.3,2237.32,0)
  FilletRadius = 0
  Length = 2923.45
  MakeFace = true
  Placement = pos=(35940.6,7398.1,0) rot=(0,0,1;3.14159rad)
  Points = (2) [(17970.3,2237.32,0),(17970.3,5160.77,0)]
  Start = (17970.3,5160.77,0)
  Subdivisions = 0
FEATURE [Part::Feature] mirror105  label="Mirror of 90cm door010"
  Placement = pos=(199.999,-2859.2,0) rot=(0,0,1;0rad)
  shape: bbox 1000 x 972 x 2e-07 mm, 5 faces, 0 solids (baked)
FEATURE [Part::Part2DObjectPython] Line029  # Draft 2D object (typed FeaturePython)
  ChamferSize = 0
  Closed = false
  End = (3408,6712,0)
  FilletRadius = 0
  Length = 2500
  MakeFace = true
  Points = (2) [(5908,6712,0),(3408,6712,0)]
  Start = (5908,6712,0)
  Subdivisions = 0
FEATURE [Part::Feature] mirror107  label="Mirror of Mirror of 90cm door017"
  Placement = pos=(-1083.97,14135.6,0) rot=(0,0,-1;1.5708rad)
  shape: bbox 972 x 1000 x 2e-07 mm, 5 faces, 0 solids (baked)
FEATURE [Part::Part2DObjectPython] Rectangle131  # Draft 2D object (typed FeaturePython)
  ChamferSize = 0
  Columns = 1
  FilletRadius = 0
  Height = 1449.19
  Length = 150.814
  MakeFace = false
  Placement = pos=(3257.19,-160,0) rot=(0,0,1;0rad)
  Rows = 1
FEATURE [Part::Feature] mirror  label="Mirror of 90cm door011"
  Placement = pos=(-1689.34,21009.5,0) rot=(0,0,-1;1.5708rad)
  shape: bbox 972 x 1000 x 2e-07 mm, 5 faces, 0 solids (baked)
FEATURE [Part::Feature] mirror108  label="Mirror of Mirror of 90cm door018"
  Placement = pos=(-3027.97,9171.99,0) rot=(0,0,-1;1.5708rad)
  shape: bbox 972 x 1000 x 2e-07 mm, 5 faces, 0 solids (baked)
FEATURE [Part::Feature] mirror109  label="Mirror of Sofa - 018"
  Placement = pos=(-672.292,15080.2,0) rot=(0,0,-1;1.5708rad)
  shape: bbox 750 x 1883 x 2e-07 mm, 2 faces, 0 solids (baked)
FEATURE [Part::Feature] mirror110  label="Mirror of Sofa - 019"
  Placement = pos=(-13673.5,-9191.81,0) rot=(0,0,1;0rad)
  shape: bbox 1400 x 750 x 2e-07 mm, 2 faces, 0 solids (baked)
FEATURE [Part::Part2DObjectPython] Rectangle136  # Draft 2D object (typed FeaturePython)
  ChamferSize = 0
  Columns = 1
  FilletRadius = 0
  Height = 9000
  Length = 5000
  MakeFace = false
  MapMode = -1
  Placement = pos=(9194.87,-20267.6,0) rot=(0,0,1;0rad)
  Rows = 1
FEATURE [Part::Part2DObjectPython] Rectangle139  # Draft 2D object (typed FeaturePython)
  ChamferSize = 0
  Columns = 1
  FilletRadius = 0
  Height = 600
  Length = 2400
  MakeFace = true
  Placement = pos=(9794.87,-15414.9,0) rot=(0,0,1;1.5708rad)
  Rows = 1
FEATURE [Part::Feature] Compound065  label="Sink 003"
  Placement = pos=(3881.67,-13417.7,0) rot=(0,0,1;0rad)
  shape: bbox 300 x 500 x 2e-07 mm, 3 faces, 0 solids (baked)
FEATURE [Part::Part2DObjectPython] Rectangle140  # Draft 2D object (typed FeaturePython)
  ChamferSize = 0
  Columns = 1
  FilletRadius = 0
  Height = 1600
  Length = 2605.46
  MakeFace = false
  Placement = pos=(9194.87,-12867.6,0) rot=(0,0,1;0rad)
  Rows = 1
FEATURE [Part::Part2DObjectPython] Rectangle141  # Draft 2D object (typed FeaturePython)
  ChamferSize = 0
  Columns = 1
  FilletRadius = 0
  Height = 1894.44
  Length = 2899.9
  MakeFace = false
  Placement = pos=(9047.65,-13014.9,0) rot=(0,0,1;0rad)
  Rows = 1
FEATURE [Part::Feature] Compound067  label="Door-90cm008"
  Placement = pos=(7359.39,-13341.5,0) rot=(0,0,1;0rad)
  shape: bbox 972 x 1000 x 2e-07 mm, 5 faces, 0 solids (baked)
FEATURE [Part::Part2DObjectPython] Rectangle142  # Draft 2D object (typed FeaturePython)
  ChamferSize = 0
  Columns = 1
  FilletRadius = 0
  Height = 1747.22
  Length = 146.164
  MakeFace = false
  Placement = pos=(10767.9,-13014.9,0) rot=(0,0,1;0rad)
  Rows = 1
FEATURE [Part::Part2DObjectPython] Line030  # Draft 2D object (typed FeaturePython)
  ChamferSize = 0
  Closed = false
  End = (9494.87,-13014.9,0)
  FilletRadius = 0
  Length = 2400
  MakeFace = true
  Placement = pos=(0,-20107.6,0) rot=(0,0,1;0rad)
  Points = (2) [(9494.87,4692.78,0),(9494.87,7092.78,0)]
  Start = (9494.87,-15414.9,0)
  Subdivisions = 0
FEATURE [Part::Part2DObjectPython] Rectangle143  # Draft 2D object (typed FeaturePython)
  ChamferSize = 0
  Columns = 1
  FilletRadius = 0
  Height = 600
  Length = 146.164
  MakeFace = false
  Placement = pos=(9194.87,-15414.9,0) rot=(0,0,-1;1.5708rad)
  Rows = 1
FEATURE [Part::Part2DObjectPython] Rectangle144  # Draft 2D object (typed FeaturePython)
  ChamferSize = 0
  Columns = 13
  FilletRadius = 0
  Height = 1573.06
  Length = 1600
  MakeFace = false
  Placement = pos=(9194.87,-12867.6,0) rot=(0.707107,0.707107,0;3.14159rad)
  Rows = 1
FEATURE [Part::Feature] mirror115  label="Mirror of Sofa - 021"
  Placement = pos=(-8834.23,-22581.1,0) rot=(0,0,1;0rad)
  shape: bbox 1400 x 750 x 2e-07 mm, 2 faces, 0 solids (baked)
FEATURE [Part::Feature] mirror121  label="Mirror of Rectangle139"
  Placement = pos=(-972,7.29e-10,0) rot=(0,0,1;0rad)
  shape: bbox 2247 x 1600 x 2e-07 mm, 0 faces, 0 solids (baked)
FEATURE [Part::Feature] mirror122  label="Mirror of Rectangle140"
  Placement = pos=(-972,7.29e-10,0) rot=(0,0,1;0rad)
  shape: bbox 2542 x 1894 x 2e-07 mm, 0 faces, 0 solids (baked)
FEATURE [Part::Feature] mirror123  label="Mirror of Mirror of Sink 010"
  Placement = pos=(-972,7.29e-10,0) rot=(0,0,1;0rad)
  shape: bbox 500 x 300 x 2e-07 mm, 3 faces, 0 solids (baked)
FEATURE [Part::Feature] mirror127  label="Mirror of Door-90cm012"
  Placement = pos=(972,-7.29e-10,0) rot=(0,0,1;0rad)
  shape: bbox 972 x 1000 x 2e-07 mm, 5 faces, 0 solids (baked)
FEATURE [Part::Part2DObjectPython] Line031  # Draft 2D object (typed FeaturePython)
  ChamferSize = 0
  Closed = false
  End = (14194.9,-15414.9,0)
  FilletRadius = 0
  Length = 4400
  MakeFace = true
  Points = (2) [(9794.87,-15414.9,0),(14194.9,-15414.9,0)]
  Start = (9794.87,-15414.9,0)
  Subdivisions = 0
FEATURE [Part::Part2DObjectPython] Line032  # Draft 2D object (typed FeaturePython)
  ChamferSize = 0
  Closed = false
  End = (9794.87,-16536.6,0)
  FilletRadius = 0
  Length = 1121.73
  MakeFace = true
  Points = (2) [(9794.87,-15414.9,0),(9794.87,-16536.6,0)]
  Start = (9794.87,-15414.9,0)
  Subdivisions = 0
FEATURE [Part::Part2DObjectPython] Line033  # Draft 2D object (typed FeaturePython)
  ChamferSize = 0
  Closed = false
  End = (10998.5,-16536.6,0)
  FilletRadius = 0
  Length = 3521.73
  MakeFace = true
  Points = (2) [(10998.5,-13014.9,0),(10998.5,-16536.6,0)]
  Start = (10998.5,-13014.9,0)
  Subdivisions = 0
FEATURE [Part::Mirroring] mirror128  label="Mirror of Mirror of Mirror of WC007"
  Base = (15617.4,-12067.6,0)
  Normal = (0,1,0)
FEATURE [Part::Mirroring] mirror129  label="Mirror of Mirror of Shower006"
  Base = (15617.4,-12067.6,0)
  Normal = (0,1,0)
FEATURE [Part::Part2DObjectPython] Line034  # Draft 2D object (typed FeaturePython)
  ChamferSize = 0
  Closed = false
  End = (15617.4,-20267.6,0)
  FilletRadius = 0
  Length = 7252.78
  MakeFace = true
  Points = (2) [(15617.4,-13014.9,0),(15617.4,-20267.6,0)]
  Start = (15617.4,-13014.9,0)
  Subdivisions = 0
FEATURE [Part::Part2DObjectPython] Line035  # Draft 2D object (typed FeaturePython)
  ChamferSize = 0
  Closed = false
  End = (15470.2,-20267.6,0)
  FilletRadius = 0
  Length = 7400
  MakeFace = true
  Points = (2) [(15470.2,-12867.6,0),(15470.2,-20267.6,0)]
  Start = (15470.2,-12867.6,0)
  Subdivisions = 0
FEATURE [Part::Part2DObjectPython] Rectangle147  # Draft 2D object (typed FeaturePython)
  ChamferSize = 0
  Columns = 1
  FilletRadius = 0
  Height = 4100
  Length = 2500
  MakeFace = true
  Placement = pos=(11370.2,-20267.6,0) rot=(0.707107,0.707107,0;3.14159rad)
  Rows = 1
  Support = -> [mirror115]
FEATURE [Part::Feature] Compound070  label="Bed-Double006"
  Placement = pos=(13768.3,-14771.1,0) rot=(0,0,1;1.5708rad)
  shape: bbox 1900 x 1400 x 2e-07 mm, 4 faces, 0 solids (baked)
FEATURE [Part::Part2DObjectPython] Rectangle148  # Draft 2D object (typed FeaturePython)
  ChamferSize = 0
  Columns = 1
  FilletRadius = 0
  Height = 600
  Length = 2500
  MakeFace = true
  Placement = pos=(15470.2,-20267.6,0) rot=(0,0,1;1.5708rad)
  Rows = 1
FEATURE [Part::Part2DObjectPython] Rectangle149  # Draft 2D object (typed FeaturePython)
  ChamferSize = 0
  Columns = 1
  FilletRadius = 0
  Height = 4752.78
  Length = 972
  MakeFace = true
  Placement = pos=(13222.9,-17767.6,0) rot=(0,0,1;0rad)
  Rows = 1
FEATURE [Part::Feature] Compound071  label="Sofa - 011"
  Placement = pos=(11288.8,-13897.5,0) rot=(0,0,1;0rad)
  shape: bbox 1883 x 750 x 2e-07 mm, 2 faces, 0 solids (baked)
FEATURE [Part::Feature] Compound072  label="Sofa - 012"
  Placement = pos=(7557.79,-14611,0) rot=(0,0,1;1.5708rad)
  shape: bbox 750 x 1400 x 2e-07 mm, 2 faces, 0 solids (baked)
FEATURE [Part::Feature] Compound074  label="dinning008"
  Placement = pos=(38896.5,-9873.61,0) rot=(0,0,1;3.14159rad)
  shape: bbox 2057 x 1200 x 2e-07 mm, 5 faces, 0 solids (baked)
FEATURE [Sketcher::SketchObject] Sketch
  sketch-geometry (13):
    g0: GeomPoint [constr] X=777.55 Y=-3734.3 Z=0
    g1: GeomPoint [constr] X=2549.74 Y=-3772.61 Z=0
    g2: GeomPoint [constr] X=289.001 Y=-5334.05 Z=0
    g3: GeomPoint [constr] X=2262.35 Y=-5516.06 Z=0
    g4: LineSegment StartX=289.001 StartY=-5334.05 StartZ=0 EndX=569.618 EndY=-4182.1 EndZ=0
    g5-g9: Circle [constr] x5 (B-spline internal-alignment scaffolding for g10; pole/knot coordinates omitted)
    g10: BSplineCurve PolesCount=5 KnotsCount=3 Degree=3 IsPeriodic=0
    g11: LineSegment StartX=569.618 StartY=-4182.1 StartZ=0 EndX=3492.32 EndY=-3505.46 EndZ=0
    g12: LineSegment StartX=4416.21 StartY=-5096.69 StartZ=0 EndX=3492.32 EndY=-3505.46 EndZ=0
  constraints (10):
    c: Coincident(g4,g2)
    c: Coincident(g5,g2)
    c: Radius(g5) = 500
    c: Equal(g5, g6-g9) x4
    c: InternalAlignment(g5-g9 -> g10) x5
    c: Coincident(g12,g9)
    c: Coincident(g11,g12)
    c: Coincident(g4,g11)
    c: Distance(g11) = 3000  'diagon'
    c: Distance(g12) = 1840
FEATURE [Part::Part2DObjectPython] DWire  # Draft 2D object (typed FeaturePython)
  Base = -> Sketch
  ChamferSize = 0
  Closed = true
  End = (4416.21,-5096.69,0)
  FilletRadius = 0
  Length = 10159.7
  MakeFace = true
  Points = (4) [(289.001,-5334.05,0),(569.618,-4182.1,0),(3492.32,-3505.46,0),(4416.21,-5096.69,0)]
  Start = (289.001,-5334.05,0)
  Subdivisions = 0
FEATURE [Part::FeaturePython] Equipment  # WARN: FeaturePython — macro-defined, semantics opaque (R4)
  EquipmentPower = 0
  HorizontalArea = 0
  MoveWithHost = false
  PerimeterLength = 0
  Role = 0
  VerticalArea = 0
FEATURE [App::DocumentObjectGroup] Group004  label="Plan Layout 1"
  Group = -> [Compound030,Shell002,Compound029,Compound027,Rectangle075,Rectangle079,Rectangle090,Compound052,Rectangle093,mirror052,mirror066,Rectangle102,mirror071,Compound061,Rectangle113,mirror088,Rectangle114,Rectangle115,Rectangle116,Rectangle117,Rectangle119,Rectangle120,Rectangle121,Rectangle122,Line025,mirror104,Line029,mirror107,Rectangle131,mirror,mirror108,Equipment]
FEATURE [App::DocumentObjectGroup] Group  label="7.5mx6m"
  Group = -> [Dimension,Dimension001,Rectangle,Group004]
FEATURE [Part::Feature] mirror130  label="Mirror of Mirror of Mirror of 90cm door010"
  Placement = pos=(12987.5,-2103.84,0) rot=(0,0,1;0rad)
  shape: bbox 1000 x 972 x 2e-07 mm, 5 faces, 0 solids (baked)
FEATURE [Part::Part2DObjectPython] Line036  # Draft 2D object (typed FeaturePython)
  ChamferSize = 0
  Closed = false
  End = (20820.3,6422.44,0)
  FilletRadius = 0
  Length = 3213.12
  MakeFace = true
  Points = (2) [(20820.3,3209.32,0),(20820.3,6422.44,0)]
  Start = (20820.3,3209.32,0)
  Subdivisions = 0
FEATURE [Part::Part2DObjectPython] Rectangle150  # Draft 2D object (typed FeaturePython)
  ChamferSize = 0
  Columns = 1
  FilletRadius = 0
  Height = 11250
  Length = 4000
  MakeFace = false
  MapMode = -1
  Placement = pos=(29266.7,-160,0) rot=(0,0,1;0rad)
  Rows = 1
FEATURE [Part::Feature] mirror136  label="Mirror of Mirror of WC006"
  Placement = pos=(-6038.49,-1437.28,0) rot=(0,0,1;0rad)
  shape: bbox 660 x 370 x 2e-07 mm, 2 faces, 0 solids (baked)
FEATURE [Part::Feature] mirror137  label="Mirror of Mirror of Sink 012"
  Placement = pos=(-6038.49,-1437.28,0) rot=(0,0,1;0rad)
  shape: bbox 500 x 300 x 2e-07 mm, 3 faces, 0 solids (baked)
FEATURE [Part::Feature] mirror138  label="Mirror of Mirror of Shower007"
  Placement = pos=(-6038.49,-1437.28,0) rot=(0,0,1;0rad)
  shape: bbox 800 x 800 x 2e-07 mm, 2 faces, 0 solids (baked)
FEATURE [Part::Feature] Compound075  label="90cm door007"
  Placement = pos=(31987.9,-1968.54,0) rot=(0,0,1;1.5708rad)
  shape: bbox 1000 x 972 x 2e-07 mm, 5 faces, 0 solids (baked)
FEATURE [Part::Part2DObjectPython] Rectangle151  # Draft 2D object (typed FeaturePython)
  ChamferSize = 0
  Columns = 1
  FilletRadius = 0
  Height = 153.543
  Length = 600
  MakeFace = false
  Placement = pos=(32666.7,1440,0) rot=(0,0,1;0rad)
  Rows = 1
FEATURE [Part::Part2DObjectPython] Line037  # Draft 2D object (typed FeaturePython)
  ChamferSize = 0
  Closed = false
  End = (32666.7,1440,0)
  FilletRadius = 0
  Length = 1000
  MakeFace = true
  Points = (2) [(32666.7,440,0),(32666.7,1440,0)]
  Start = (32666.7,440,0)
  Subdivisions = 0
FEATURE [Part::Part2DObjectPython] Line039  # Draft 2D object (typed FeaturePython)
  ChamferSize = 0
  Closed = false
  End = (32666.7,440,0)
  FilletRadius = 0
  Length = 999.133
  MakeFace = true
  Points = (2) [(31667.6,440,0),(32666.7,440,0)]
  Start = (31667.6,440,0)
  Subdivisions = 0
FEATURE [Part::Feature] Compound076  label="Sink 004"
  Placement = pos=(23353.5,3796.19,0) rot=(0,0,1;0rad)
  shape: bbox 300 x 500 x 2e-07 mm, 3 faces, 0 solids (baked)
FEATURE [Part::Part2DObjectPython] Line040  # Draft 2D object (typed FeaturePython)
  ChamferSize = 0
  Closed = false
  End = (28966.7,4199,0)
  FilletRadius = 0
  Length = 2605.46
  MakeFace = true
  Placement = pos=(19471.8,-2893.78,0) rot=(0,0,1;0rad)
  Points = (2) [(9494.87,4487.32,0),(9494.87,7092.78,0)]
  Start = (28966.7,1593.54,0)
  Subdivisions = 0
FEATURE [Part::Part2DObjectPython] Rectangle152  # Draft 2D object (typed FeaturePython)
  ChamferSize = 0
  Columns = 1
  FilletRadius = 0
  Height = 600
  Length = 2605.46
  MakeFace = true
  Placement = pos=(29266.7,1593.54,0) rot=(0,0,1;1.5708rad)
  Rows = 1
FEATURE [Part::Part2DObjectPython] Rectangle153  # Draft 2D object (typed FeaturePython)
  ChamferSize = 0
  Columns = 1
  FilletRadius = 0
  Height = 800
  Length = 1800.87
  MakeFace = true
  Placement = pos=(29266.7,3399,0) rot=(0,0,1;0rad)
  Rows = 1
FEATURE [Part::Part2DObjectPython] Rectangle154  # Draft 2D object (typed FeaturePython)
  ChamferSize = 0
  Columns = 1
  FilletRadius = 0
  Height = 450
  Length = 450
  MakeFace = true
  Placement = pos=(31217.6,4396.25,0) rot=(0,0,1;0rad)
  Rows = 1
  Support = -> [Compound051]
FEATURE [Part::FeaturePython] Array  # Draft array (typed FeaturePython)
  Angle = 360
  ArrayType = 0
  Axis = (0,0,1)
  Base = -> Rectangle154
  Center = (0,0,0)
  Fuse = false
  IntervalAxis = (0,0,0)
  IntervalX = (-650,0,0)
  IntervalY = (0,0,0)
  IntervalZ = (0,0,0)
  NumberPolar = 1
  NumberX = 3
  NumberY = 0
  NumberZ = 0
  Placement = pos=(-600,2e-12,0) rot=(0,0,1;0rad)
FEATURE [Part::Part2DObjectPython] DWire008  # Draft 2D object (typed FeaturePython)
  ChamferSize = 0
  Closed = true
  End = (32666.7,1440,0)
  FilletRadius = 0
  Length = 23193.2
  MakeFace = true
  Points = (16) [(32666.7,1593.54,0),(33420.3,1593.54,0),(33420.3,-313.543,0),(29113.2,-313.543,0),(29113.2,1593.54,0),(31667.6,1593.54,0),(31667.6,1440,0),+9 more]
  Start = (32666.7,1593.54,0)
  Subdivisions = 0
FEATURE [Part::Part2DObjectPython] DWire009  # Draft 2D object (typed FeaturePython)
  ChamferSize = 0
  Closed = true
  End = (32666.7,440,0)
  FilletRadius = 0
  Length = 6398.27
  MakeFace = true
  Points = (6) [(32666.7,1440,0),(33266.7,1440,0),(33266.7,-160,0),(31667.6,-160,0),(31667.6,440,0),(32666.7,440,0)]
  Start = (32666.7,1440,0)
  Subdivisions = 0
FEATURE [Part::Feature] Compound077  label="Bed-Double007"
  Placement = pos=(30388.1,13681.1,0) rot=(0,0,1;1.5708rad)
  shape: bbox 1900 x 1400 x 2e-07 mm, 4 faces, 0 solids (baked)
FEATURE [Part::Part2DObjectPython] Rectangle157  # Draft 2D object (typed FeaturePython)
  ChamferSize = 0
  Columns = 1
  FilletRadius = 0
  Height = 3000
  Length = 4000
  MakeFace = true
  Placement = pos=(29266.7,8090,0) rot=(0,0,1;0rad)
  Rows = 1
FEATURE [Part::Part2DObjectPython] Rectangle158  # Draft 2D object (typed FeaturePython)
  ChamferSize = 0
  Columns = 1
  FilletRadius = 0
  Height = 3303.44
  Length = 4303.44
  MakeFace = true
  Placement = pos=(29115,7938.28,0) rot=(0,0,1;0rad)
  Rows = 1
FEATURE [Part::Part2DObjectPython] Rectangle161  # Draft 2D object (typed FeaturePython)
  ChamferSize = 0
  Columns = 1
  FilletRadius = 0
  Height = 600.001
  Length = 18
  MakeFace = true
  Placement = pos=(31748.7,10490,0) rot=(0,0,1;0rad)
  Rows = 1
FEATURE [Part::Part2DObjectPython] Rectangle163  # Draft 2D object (typed FeaturePython)
  ChamferSize = 0
  Columns = 1
  FilletRadius = 0
  Height = 600.001
  Length = 18
  MakeFace = true
  Placement = pos=(31730.7,10490,0) rot=(0,0,1;0rad)
  Rows = 1
FEATURE [Part::Part2DObjectPython] Rectangle166  # Draft 2D object (typed FeaturePython)
  ChamferSize = 0
  Columns = 1
  FilletRadius = 0
  Height = 6344.73
  Length = 4000
  MakeFace = true
  Placement = pos=(28666.7,1593.54,0) rot=(0,0,1;0rad)
  Rows = 1
FEATURE [Part::Part2DObjectPython] Rectangle167  # Draft 2D object (typed FeaturePython)
  ChamferSize = 0
  Columns = 1
  FilletRadius = 0
  Height = 6651.82
  Length = 4307.09
  MakeFace = true
  Placement = pos=(28513.2,1440,0) rot=(0,0,1;0rad)
  Rows = 1
FEATURE [Part::Feature] Clone002  label="Clone of Door-90cm006"
  Placement = pos=(29258.2,7617.96,0) rot=(0,0,1;0rad)
  shape: bbox 972 x 1000 x 2e-07 mm, 5 faces, 0 solids (baked)
FEATURE [Part::Feature] Compound078  label="Sofa - 013"
  Placement = pos=(31064.7,9627.64,0) rot=(0,0,1;0rad)
  shape: bbox 1883 x 750 x 2e-07 mm, 2 faces, 0 solids (baked)
FEATURE [Part::Feature] mirror139  label="Mirror of Sofa - 022"
  Placement = pos=(23505.9,24636.4,0) rot=(0,0,-1;1.5708rad)
  shape: bbox 750 x 1883 x 2e-07 mm, 2 faces, 0 solids (baked)
FEATURE [Part::Part2DObjectPython] Rectangle168  # Draft 2D object (typed FeaturePython)
  ChamferSize = 0
  Columns = 1
  FilletRadius = 0
  Height = 450
  Length = 450
  MakeFace = true
  Placement = pos=(28931.8,7140.28,0) rot=(0,0,1;0.463648rad)
  Rows = 1
FEATURE [Part::Part2DObjectPython] Rectangle169  # Draft 2D object (typed FeaturePython)
  ChamferSize = 0
  Columns = 1
  FilletRadius = 0
  Height = 950
  Length = 950
  MakeFace = true
  Placement = pos=(29968.3,5699.81,0) rot=(0.707107,0.707107,0;3.14159rad)
  Rows = 1
FEATURE [Part::Part2DObjectPython] DWire010  # Draft 2D object (typed FeaturePython)
  ChamferSize = 0
  Closed = true
  End = (28513.2,8091.82,0)
  FilletRadius = 0
  Length = 34121.1
  MakeFace = true
  Points = (12) [(29115,8091.82,0),(29115,11241.7,0),(33418.4,11241.7,0),(33418.4,7938.28,0),(32820.3,7938.28,0),(32820.3,1593.54,0),(33420.3,1593.54,0),+5 more]
  Start = (29115,8091.82,0)
  Subdivisions = 0
FEATURE [Part::Part2DObjectPython] DWire011  # Draft 2D object (typed FeaturePython)
  ChamferSize = 0
  Closed = true
  End = (28666.7,7938.28,0)
  FilletRadius = 0
  Length = 32892.7
  MakeFace = true
  Points = (12) [(29268.5,7938.28,0),(29268.5,11088.2,0),(33264.9,11088.2,0),(33264.9,8091.82,0),(32666.7,8091.82,0),(32666.7,1440,0),(33266.7,1440,0),+5 more]
  Start = (29268.5,7938.28,0)
  Subdivisions = 0
FEATURE [Part::Feature] mirror145  label="Mirror of Mirror of Mirror of Mirror of 90cm door012"
  Placement = pos=(-46.4568,2e-12,0) rot=(0,0,1;0rad)
  shape: bbox 1000 x 972 x 2e-07 mm, 5 faces, 0 solids (baked)
FEATURE [Part::Feature] mirror146  label="Mirror of 90cm door014"
  Placement = pos=(-46.4568,2e-12,0) rot=(0,0,1;0rad)
  shape: bbox 1000 x 972 x 2e-07 mm, 5 faces, 0 solids (baked)
FEATURE [Part::Feature] mirror147  label="Mirror of Mirror of Mirror of Mirror of 90cm door013"
  Placement = pos=(-46.4568,2e-12,0) rot=(0,0,1;0rad)
  shape: bbox 1000 x 972 x 2e-07 mm, 5 faces, 0 solids (baked)
FEATURE [Part::Feature] mirror148  label="Mirror of 90cm door015"
  Placement = pos=(-46.4568,2e-12,0) rot=(0,0,1;0rad)
  shape: bbox 1000 x 972 x 2e-07 mm, 5 faces, 0 solids (baked)
FEATURE [Part::Part2DObjectPython] DWire012  # Draft 2D object (typed FeaturePython)
  ChamferSize = 0
  Closed = true
  End = (33418.4,7938.28,0)
  FilletRadius = 0
  Length = 22097.5
  MakeFace = true
  Points = (8) [(33418.4,9590,0),(34919,9590,0),(34919,640,0),(33420.3,640,0),(33420.3,1593.54,0),(32820.3,1593.54,0),(32820.3,7938.28,0),(33418.4,7938.28,0)]
  Start = (33418.4,9590,0)
  Subdivisions = 0
FEATURE [Part::Feature] mirror152  label="Mirror of Shower005"
  Placement = pos=(-356.748,4.002e-09,0) rot=(0,0,1;0rad)
  shape: bbox 800 x 800 x 2e-07 mm, 2 faces, 0 solids (baked)
FEATURE [Part::Feature] mirror153  label="Mirror of Mirror of WC008"
  Placement = pos=(-356.748,4.002e-09,0) rot=(0,0,1;0rad)
  shape: bbox 660 x 370 x 2e-07 mm, 2 faces, 0 solids (baked)
FEATURE [Part::Part2DObjectPython] DWire013  # Draft 2D object (typed FeaturePython)
  ChamferSize = 0
  Closed = true
  End = (10797.3,8840,0)
  FilletRadius = 0
  Length = 6404.88
  MakeFace = true
  Points = (6) [(10797.3,8212,0),(9794.87,8212,0),(9794.87,7240,0),(9194.87,7240,0),(9194.87,8840,0),(10797.3,8840,0)]
  Start = (10797.3,8212,0)
  Subdivisions = 0
FEATURE [Part::Part2DObjectPython] DWire014  # Draft 2D object (typed FeaturePython)
  ChamferSize = 0
  Closed = true
  End = (9194.87,7240,0)
  FilletRadius = 0
  Length = 23110.2
  MakeFace = true
  Points = (16) [(9794.87,7240,0),(9794.87,7092.78,0),(9047.65,7092.78,0),(9047.65,8987.22,0),(13338,8987.22,0),(13338,7092.78,0),(10796.3,7092.78,0),(10796.3,7240,0),+8 more]
  Start = (9794.87,7240,0)
  Subdivisions = 0
FEATURE [Part::Part2DObjectPython] Rectangle170  # Draft 2D object (typed FeaturePython)
  ChamferSize = 0
  Columns = 1
  FilletRadius = 0
  Height = 2610
  Length = 570
  MakeFace = true
  Placement = pos=(13338,7092.78,0) rot=(0,0,1;0rad)
  Rows = 1
FEATURE [Part::Feature] mirror158  label="Mirror of Mirror of Mirror of 90cm door012"
  Placement = pos=(-23936.2,-2627.64,0) rot=(0,0,1;0rad)
  shape: bbox 1000 x 972 x 2e-07 mm, 5 faces, 0 solids (baked)
FEATURE [Part::Part2DObjectPython] Rectangle173  # Draft 2D object (typed FeaturePython)
  ChamferSize = 0
  Columns = 1
  FilletRadius = 0
  Height = 2605.46
  Length = 5589.69
  MakeFace = true
  Placement = pos=(9194.87,1881.87,0) rot=(0,0,1;0rad)
  Rows = 1
FEATURE [Part::Part2DObjectPython] Rectangle177  # Draft 2D object (typed FeaturePython)
  ChamferSize = 0
  Columns = 1
  FilletRadius = 0
  Height = 2041.87
  Length = 4100
  MakeFace = true
  Placement = pos=(15759.3,-6724.47,0) rot=(0,0,1;0rad)
  Rows = 1
FEATURE [Part::Feature] mirror165  label="Mirror of Rectangle175"
  Placement = pos=(-3623.17,-7185.78,0) rot=(0,0,1;0rad)
  shape: bbox 1801 x 800 x 2e-07 mm, 1 faces, 0 solids (baked)
FEATURE [Part::Feature] mirror166  label="Mirror of Array003"
  Placement = pos=(-3623.17,-7185.78,0) rot=(0,0,1;0rad)
  shape: bbox 1750 x 450 x 2e-07 mm, 3 faces, 0 solids (baked)
FEATURE [Part::Part2DObjectPython] Rectangle182  # Draft 2D object (typed FeaturePython)
  ChamferSize = 0
  Columns = 1
  FilletRadius = 0
  Height = 2041.87
  Length = 4100
  MakeFace = true
  Placement = pos=(21589.8,-6130.95,0) rot=(0,0,1;0rad)
  Rows = 1
FEATURE [Part::Part2DObjectPython] Rectangle187  # Draft 2D object (typed FeaturePython)
  ChamferSize = 0
  Columns = 1
  FilletRadius = 0
  Height = 6589.69
  Length = 395.411
  MakeFace = true
  Placement = pos=(14389.2,3487.32,0) rot=(0,0,1;0rad)
  Rows = 1
FEATURE [Part::Part2DObjectPython] Rectangle188  # Draft 2D object (typed FeaturePython)
  ChamferSize = 0
  Columns = 1
  FilletRadius = 0
  Height = 3306.02
  Length = 6894.85
  MakeFace = true
  Placement = pos=(14236.6,10829.6,0) rot=(0,0,-1;1.5708rad)
  Rows = 1
FEATURE [Part::Feature] mirror194  label="Mirror of DWire016"
  Placement = pos=(17329.4,-811.721,0) rot=(0,0,1;1.5708rad)
  shape: bbox 1894 x 4290 x 2e-07 mm, 1 faces, 0 solids (baked)
FEATURE [Part::Feature] mirror195  label="Mirror of Mirror of Shower009"
  Placement = pos=(11366.6,-31212.4,0) rot=(0,0,1;1.5708rad)
  shape: bbox 800 x 800 x 2e-07 mm, 2 faces, 0 solids (baked)
FEATURE [Part::Feature] mirror196  label="Mirror of Mirror of WC010"
  Placement = pos=(11366.6,-31212.4,0) rot=(0,0,1;1.5708rad)
  shape: bbox 370 x 660 x 2e-07 mm, 2 faces, 0 solids (baked)
FEATURE [Part::Feature] mirror197  label="Mirror of Sink 012"
  Placement = pos=(-10744.6,5607.34,0) rot=(0,0,1;0rad)
  shape: bbox 300 x 500 x 2e-07 mm, 3 faces, 0 solids (baked)
FEATURE [Part::Feature] mirror198  label="Mirror of Mirror of Mirror of 90cm door022"
  Placement = pos=(14430.5,-1492.71,0) rot=(0,0,1;1.5708rad)
  shape: bbox 972 x 1000 x 2e-07 mm, 5 faces, 0 solids (baked)
FEATURE [Part::Feature] mirror199  label="Mirror of DWire017"
  Placement = pos=(17329.4,-4311.05,0) rot=(0,0,1;1.5708rad)
  shape: bbox 1600 x 1602 x 2e-07 mm, 1 faces, 0 solids (baked)
FEATURE [Part::Feature] mirror200  label="Mirror of Rectangle184"
  Placement = pos=(46532.5,-7076,0) rot=(0,0,1;1.5708rad)
  shape: bbox 2500 x 600 x 2e-07 mm, 1 faces, 0 solids (baked)
FEATURE [Part::Feature] mirror201  label="Mirror of Rectangle185"
  Placement = pos=(46532.5,-7076,0) rot=(0,0,1;1.5708rad)
  shape: bbox 1500 x 600 x 2e-07 mm, 1 faces, 0 solids (baked)
FEATURE [Part::Feature] mirror210  label="Mirror of Sofa - 024"
  Placement = pos=(0,7619.69,0) rot=(0,0,1;0rad)
  shape: bbox 1883 x 750 x 2e-07 mm, 2 faces, 0 solids (baked)
FEATURE [Part::Feature] mirror211  label="Mirror of Rectangle187"
  Placement = pos=(0,7619.69,0) rot=(0,0,1;0rad)
  shape: bbox 603.7 x 603.7 x 2e-07 mm, 1 faces, 0 solids (baked)
FEATURE [Part::Feature] mirror212  label="Mirror of Rectangle188"
  Placement = pos=(0,7619.69,0) rot=(0,0,1;0rad)
  shape: bbox 950 x 950 x 2e-07 mm, 1 faces, 0 solids (baked)
FEATURE [Part::Feature] mirror213  label="Mirror of Mirror of Sofa - 024"
  Placement = pos=(0,7619.69,0) rot=(0,0,1;0rad)
  shape: bbox 750 x 1883 x 2e-07 mm, 2 faces, 0 solids (baked)
FEATURE [Part::Feature] mirror214  label="Mirror of Mirror of Array006"
  Placement = pos=(0,7619.69,0) rot=(0,0,1;0rad)
  shape: bbox 1750 x 450 x 2e-07 mm, 3 faces, 0 solids (baked)
FEATURE [Part::Feature] mirror215  label="Mirror of Mirror of Rectangle178"
  Placement = pos=(0,7619.69,0) rot=(0,0,1;0rad)
  shape: bbox 1801 x 800 x 2e-07 mm, 1 faces, 0 solids (baked)
FEATURE [Part::Feature] mirror216  label="Mirror of Line045"
  Placement = pos=(0,7619.69,0) rot=(0,0,1;0rad)
  shape: bbox 3001 x 0.0004885 x 2e-07 mm, 0 faces, 0 solids (baked)
FEATURE [Part::Feature] mirror217  label="Mirror of Rectangle189"
  Placement = pos=(0,7619.69,0) rot=(0,0,1;0rad)
  shape: bbox 3001 x 600 x 2e-07 mm, 1 faces, 0 solids (baked)
FEATURE [Part::Part2DObjectPython] Rectangle193  # Draft 2D object (typed FeaturePython)
  ChamferSize = 0
  Columns = 1
  FilletRadius = 0
  Height = 3306.02
  Length = 6894.85
  MakeFace = true
  Placement = pos=(10003.5,24885.3,0) rot=(0,0,-1;1.5708rad)
  Rows = 1
FEATURE [Part::Part2DObjectPython] Rectangle194  # Draft 2D object (typed FeaturePython)
  ChamferSize = 0
  Columns = 1
  FilletRadius = 0
  Height = 3000.87
  Length = 6589.69
  MakeFace = true
  Placement = pos=(10156.1,24732.7,0) rot=(0,0,-1;1.5708rad)
  Rows = 1
FEATURE [Part::Part2DObjectPython] Line048  # Draft 2D object (typed FeaturePython)
  ChamferSize = 0
  Closed = false
  End = (13157,24432.7,0)
  FilletRadius = 0
  Length = 3000.87
  MakeFace = true
  Placement = pos=(7798.54,17392.7,0) rot=(0,0,1;0rad)
  Points = (2) [(2357.57,7040,0),(5358.43,7040,0)]
  Start = (10156.1,24432.7,0)
  Subdivisions = 0
FEATURE [Part::Part2DObjectPython] Rectangle195  # Draft 2D object (typed FeaturePython)
  ChamferSize = 0
  Columns = 1
  FilletRadius = 0
  Height = 600
  Length = 3000.87
  MakeFace = true
  Placement = pos=(10156.1,24132.7,0) rot=(0,0,1;0rad)
  Rows = 1
FEATURE [Part::Feature] mirror218  label="Mirror of Rectangle190"
  Placement = pos=(672.106,12578.1,0) rot=(0,0,1;0rad)
  shape: bbox 1801 x 800 x 2e-07 mm, 1 faces, 0 solids (baked)
FEATURE [Part::Feature] mirror219  label="Mirror of Array006"
  Placement = pos=(672.106,12578.1,0) rot=(0,0,1;0rad)
  shape: bbox 1750 x 450 x 2e-07 mm, 3 faces, 0 solids (baked)
FEATURE [Part::Feature] mirror220  label="Mirror of Sofa - 025"
  Placement = pos=(18317.7,1443.14,0) rot=(0,0,1;1.5708rad)
  shape: bbox 750 x 1883 x 2e-07 mm, 2 faces, 0 solids (baked)
FEATURE [Part::Part2DObjectPython] Rectangle196  # Draft 2D object (typed FeaturePython)
  ChamferSize = 0
  Columns = 1
  FilletRadius = 0
  Height = 950
  Length = 950
  MakeFace = true
  Placement = pos=(11007.4,19358.5,0) rot=(0.707107,0.707107,0;3.14159rad)
  Rows = 1
FEATURE [Part::Part2DObjectPython] Rectangle197  # Draft 2D object (typed FeaturePython)
  ChamferSize = 0
  Columns = 1
  FilletRadius = 0
  Height = 450
  Length = 450
  MakeFace = true
  Placement = pos=(12891.9,18939.3,0) rot=(0,0,1;3.60524rad)
  Rows = 1
FEATURE [Part::Feature] Compound087  label="Sofa - 016"
  Placement = pos=(10759,16451.9,0) rot=(0,0,1;3.14159rad)
  shape: bbox 1883 x 750 x 2e-07 mm, 2 faces, 0 solids (baked)
FEATURE [Part::Feature] mirror222  label="Mirror of Rectangle191"
  Placement = pos=(-2265.75,-6269.37,0) rot=(0,0,1;0rad)
  shape: bbox 603.7 x 603.7 x 2e-07 mm, 1 faces, 0 solids (baked)
FEATURE [Part::Feature] mirror227  label="Mirror of Line046"
  Placement = pos=(0,-6294.85,0) rot=(0,0,1;0rad)
  shape: bbox 3001 x 0.0004885 x 2e-07 mm, 0 faces, 0 solids (baked)
FEATURE [Part::Feature] mirror228  label="Mirror of Rectangle193"
  Placement = pos=(0,-6294.85,0) rot=(0,0,1;0rad)
  shape: bbox 3001 x 600 x 2e-07 mm, 1 faces, 0 solids (baked)
FEATURE [Part::Feature] mirror229  label="Mirror of Mirror of Sink 013"
  Placement = pos=(-20865.6,2960.04,0) rot=(0,0,1;0rad)
  shape: bbox 500 x 300 x 2e-07 mm, 3 faces, 0 solids (baked)
FEATURE [Part::Part2DObjectPython] DWire015  # Draft 2D object (typed FeaturePython)
  ChamferSize = 0
  Closed = true
  End = (14236.6,3934.75,0)
  FilletRadius = 0
  Length = 32200.5
  MakeFace = true
  Points = (6) [(14236.6,10829.6,0),(17542.6,10829.6,0),(17542.6,7239.09,0),(23442,7239.09,0),(23442,3934.75,0),(14236.6,3934.75,0)]
  Start = (14236.6,10829.6,0)
  Subdivisions = 0
FEATURE [Part::Compound] Compound088
  Links = -> [mirror199,mirror194,mirror197,mirror195,mirror196,mirror198]
FEATURE [Part::Feature] Compound089
  Placement = pos=(6147.87,19166.4,0) rot=(0,0,-1;1.5708rad)
  shape: bbox 4290 x 1894 x 2e-07 mm, 14 faces, 0 solids (baked)
FEATURE [Part::Feature] mirror232  label="Mirror of Compound091"
  Placement = pos=(22194.4,684.266,0) rot=(0,0,1;1.5708rad)
  shape: bbox 1894 x 4290 x 2e-07 mm, 14 faces, 0 solids (baked)
FEATURE [Part::Mirroring] mirror233  label="Mirror of Mirror of Compound091"
  Base = (13264.6,10777.7,0)
  Normal = (-1,-9.0606e-08,0)
  Source = -> mirror232
FEATURE [Part::Feature] mirror264  label="Mirror of Mirror of Rectangle202"
  Placement = pos=(18066.9,25634.9,0) rot=(0,0,-1;1.5708rad)
  shape: bbox 600 x 2500 x 2e-07 mm, 1 faces, 0 solids (baked)
FEATURE [Part::Feature] mirror265  label="Mirror of Mirror of Mirror of Mirror of Mirror of Rectangle186"
  Placement = pos=(18066.9,25634.9,0) rot=(0,0,-1;1.5708rad)
  shape: bbox 600 x 1500 x 2e-07 mm, 1 faces, 0 solids (baked)
FEATURE [Part::Feature] mirror266  label="Mirror of Mirror of Mirror of Mirror of Mirror of Rectangle187"
  Placement = pos=(16697.5,25676.9,0) rot=(0,0,-1;1.5708rad)
  shape: bbox 603.7 x 603.7 x 2e-07 mm, 1 faces, 0 solids (baked)
FEATURE [Part::Feature] mirror268  label="Mirror of Mirror of Rectangle203"
  Placement = pos=(15666.9,25634.9,0) rot=(0,0,-1;1.5708rad)
  shape: bbox 3000 x 4000 x 2e-07 mm, 1 faces, 0 solids (baked)
FEATURE [Part::Feature] mirror269  label="Mirror of Mirror of Rectangle204"
  Placement = pos=(15666.9,25634.9,0) rot=(0,0,-1;1.5708rad)
  shape: bbox 3304 x 4304 x 2e-07 mm, 1 faces, 0 solids (baked)
FEATURE [Part::Feature] mirror243  label="Mirror of Mirror of Mirror of Compound094"
  Placement = pos=(13235.4,27120.8,0) rot=(0,0,-1;1.5708rad)
  shape: bbox 4290 x 1894 x 2e-07 mm, 14 faces, 0 solids (baked)
FEATURE [Part::Mirroring] mirror271  label="Mirror of DWire018"
  Base = (19642.4,15273.8,0)
  Normal = (-1,1.65871e-06,0)
  Placement = pos=(2334.65,2976.15,0) rot=(0,0,1;0rad)
FEATURE [Part::Feature] mirror272  label="Mirror of DWire019"
  Placement = pos=(37037.8,19208.6,0) rot=(0,0,1;3.14159rad)
  shape: bbox 1894 x 2542 x 2e-07 mm, 1 faces, 0 solids (baked)
FEATURE [Part::Mirroring] mirror274  label="Mirror of Mirror of Mirror of Rectangle179"
  Base = (11694.9,8840,0)
  Normal = (-1,0,0)
  Placement = pos=(8389.43,-2e-12,0) rot=(0,0,1;0rad)
FEATURE [Part::Mirroring] mirror275  label="Mirror of Mirror of Mirror of Array007"
  Base = (11694.9,8840,0)
  Normal = (-1,0,0)
  Placement = pos=(8389.43,-2e-12,0) rot=(0,0,1;0rad)
FEATURE [Part::Mirroring] mirror278  label="Mirror of Mirror of Mirror of Sofa - 025"
  Base = (11694.9,8840,0)
  Normal = (-1,0,0)
  Placement = pos=(8389.43,-2e-12,0) rot=(0,0,1;0rad)
FEATURE [Part::Mirroring] mirror279  label="Mirror of Mirror of Rectangle192"
  Base = (11694.9,8840,0)
  Normal = (-1,0,0)
  Placement = pos=(8389.43,-2e-12,0) rot=(0,0,1;0rad)
FEATURE [Part::Mirroring] mirror280  label="Mirror of Mirror of Sofa - 026"
  Base = (11694.9,8840,0)
  Normal = (-1,0,0)
  Placement = pos=(8389.43,-2e-12,0) rot=(0,0,1;0rad)
FEATURE [Part::Part2DObjectPython] Rectangle198  # Draft 2D object (typed FeaturePython)
  ChamferSize = 0
  Columns = 1
  FilletRadius = 0
  Height = 2428
  Length = 151.722
  MakeFace = true
  Placement = pos=(31694.7,7938.28,0) rot=(0,0,1;1.5708rad)
  Rows = 1
FEATURE [Part::Part2DObjectPython] Rectangle199  # Draft 2D object (typed FeaturePython)
  ChamferSize = 0
  Columns = 1
  FilletRadius = 0
  Height = 2400.87
  Length = 153.543
  MakeFace = true
  Placement = pos=(31667.6,1440,0) rot=(0,0,1;1.5708rad)
  Rows = 1
FEATURE [Part::Part2DObjectPython] Rectangle200  # Draft 2D object (typed FeaturePython)
  ChamferSize = 0
  Columns = 1
  FilletRadius = 0
  Height = 1895.83
  Length = 1894.44
  MakeFace = true
  Placement = pos=(26135.7,8709.39,0) rot=(0,0,1;1.5708rad)
  Rows = 1
FEATURE [Part::Feature] mirror290  label="Mirror of Mirror of Mirror of Mirror of Mirror of Rectangle188"
  Placement = pos=(28065.7,30959.4,0) rot=(0,0,-1;1.5708rad)
  shape: bbox 603.7 x 603.7 x 2e-07 mm, 1 faces, 0 solids (baked)
FEATURE [Part::Part2DObjectPython] DWire018  # Draft 2D object (typed FeaturePython)
  ChamferSize = 0
  Closed = true
  End = (19142.6,10682.4,0)
  FilletRadius = 0
  Length = 14915.4
  MakeFace = true
  Placement = pos=(32021.8,-13249.1,0) rot=(0,0,1;1.57079rad)
  Points = (10) [(21536.9,12879.3,0),(21536.9,12732,0),(24078.6,12732,0),(24078.6,14626.5,0),(21537.9,14626.5,0),(21537.9,13851.3,0),(21684.1,13851.3,0),+3 more]
  Start = (19142.6,8287.82,0)
  Subdivisions = 0
FEATURE [Part::Feature] mirror291  label="Mirror of Mirror of 90cm door019"
  Placement = pos=(14801.4,16267.9,0) rot=(0,0,-1;1.5708rad)
  shape: bbox 972 x 1000 x 2e-07 mm, 5 faces, 0 solids (baked)
FEATURE [Part::Feature] Compound090  label="Bed-Double008"
  Placement = pos=(25097.1,6165.85,0) rot=(0,0,1;0rad)
  shape: bbox 1400 x 1900 x 2e-07 mm, 4 faces, 0 solids (baked)
FEATURE [Part::Feature] mirror293  label="Mirror of Mirror of Mirror of Compound095"
  Placement = pos=(38467.4,23575.3,0) rot=(0,0,1;3.14159rad)
  shape: bbox 1894 x 4290 x 2e-07 mm, 14 faces, 0 solids (baked)
FEATURE [Part::Feature] mirror294  label="Mirror of Mirror of Mirror of Compound096"
  Placement = pos=(31784.1,17382.4,0) rot=(0,0,1;3.14159rad)
  shape: bbox 1894 x 4290 x 2e-07 mm, 14 faces, 0 solids (baked)
FEATURE [Part::Feature] mirror301  label="Mirror of 90cm door019"
  Placement = pos=(-580.501,3145.75,0) rot=(0,0,1;0rad)
  shape: bbox 1000 x 972 x 2e-07 mm, 5 faces, 0 solids (baked)
FEATURE [Part::Part2DObjectPython] Rectangle202  # Draft 2D object (typed FeaturePython)
  ChamferSize = 0
  Columns = 1
  FilletRadius = 0
  Height = 152.175
  Length = 1352.17
  MakeFace = true
  Placement = pos=(19289.8,8092.27,0) rot=(0,0,1;1.5708rad)
  Rows = 1
FEATURE [Part::Part2DObjectPython] Rectangle203  # Draft 2D object (typed FeaturePython)
  ChamferSize = 0
  Columns = 1
  FilletRadius = 0
  Height = 3000.87
  Length = 6589.69
  MakeFace = true
  Placement = pos=(14389.2,10677,0) rot=(0,0,-1;1.5708rad)
  Rows = 1
FEATURE [Part::Part2DObjectPython] Rectangle204  # Draft 2D object (typed FeaturePython)
  ChamferSize = 0
  Columns = 1
  FilletRadius = 0
  Height = 152.174
  Length = 1748.6
  MakeFace = true
  Placement = pos=(17542.6,9444.45,0) rot=(0,0,1;0rad)
  Rows = 1
FEATURE [Part::Part2DObjectPython] Rectangle205  # Draft 2D object (typed FeaturePython)
  ChamferSize = 0
  Columns = 1
  FilletRadius = 0
  Height = 152.174
  Length = 967.049
  MakeFace = true
  Placement = pos=(18170.6,8092.27,0) rot=(0,0,1;0rad)
  Rows = 1
FEATURE [Part::Part2DObjectPython] Rectangle206  # Draft 2D object (typed FeaturePython)
  ChamferSize = 0
  Columns = 1
  FilletRadius = 0
  Height = 1895.83
  Length = 1894.44
  MakeFace = true
  Placement = pos=(22780.1,9681.22,0) rot=(0,0,1;1.5708rad)
  Rows = 1
FEATURE [Part::Feature] mirror303  label="Mirror of Mirror of 90cm door021"
  Placement = pos=(13201.4,17477.3,0) rot=(0,0,-1;1.5708rad)
  shape: bbox 972 x 1000 x 2e-07 mm, 5 faces, 0 solids (baked)
FEATURE [Part::Feature] mirror304  label="Mirror of Mirror of Mirror of 90cm door025"
  Placement = pos=(6403.77,346.164,0) rot=(0,0,1;0rad)
  shape: bbox 1000 x 972 x 2e-07 mm, 5 faces, 0 solids (baked)
FEATURE [Part::Feature] mirror307  label="Mirror of Mirror of DWire022"
  Placement = pos=(344.001,0,0) rot=(0,0,1;0rad)
  shape: bbox 1894 x 2542 x 2e-07 mm, 1 faces, 0 solids (baked)
FEATURE [Part::Feature] mirror308  label="Mirror of Mirror of Mirror of Mirror of 90cm door025"
  Placement = pos=(344.001,0,0) rot=(0,0,1;0rad)
  shape: bbox 972 x 1000 x 2e-07 mm, 5 faces, 0 solids (baked)
FEATURE [Part::Part2DObjectPython] Rectangle207  # Draft 2D object (typed FeaturePython)
  ChamferSize = 0
  Columns = 1
  FilletRadius = 0
  Height = 3306.02
  Length = 6894.85
  MakeFace = true
  Placement = pos=(29893.9,-8522.47,0) rot=(0,0,-1;1.5708rad)
  Rows = 1
FEATURE [Part::Feature] mirror309  label="Mirror of Rectangle194"
  Placement = pos=(13391.6,-25621.4,0) rot=(0,0,1;0rad)
  shape: bbox 603.7 x 603.7 x 2e-07 mm, 1 faces, 0 solids (baked)
FEATURE [Part::Feature] mirror310  label="Mirror of Line047"
  Placement = pos=(15657.4,-25646.9,0) rot=(0,0,1;0rad)
  shape: bbox 3001 x 0.0004885 x 2e-07 mm, 0 faces, 0 solids (baked)
FEATURE [Part::Feature] mirror311  label="Mirror of Rectangle195"
  Placement = pos=(15657.4,-25646.9,0) rot=(0,0,1;0rad)
  shape: bbox 3001 x 600 x 2e-07 mm, 1 faces, 0 solids (baked)
FEATURE [Part::Feature] mirror312  label="Mirror of Mirror of Sink 014"
  Placement = pos=(-5208.27,-16392,0) rot=(0,0,1;0rad)
  shape: bbox 500 x 300 x 2e-07 mm, 3 faces, 0 solids (baked)
FEATURE [Part::Feature] mirror318  label="Mirror of Mirror of Mirror of Rectangle180"
  Placement = pos=(24046.8,-19352.1,0) rot=(0,0,1;0rad)
  shape: bbox 1801 x 800 x 2e-07 mm, 1 faces, 0 solids (baked)
FEATURE [Part::Feature] mirror319  label="Mirror of Mirror of Mirror of Array008"
  Placement = pos=(24046.8,-19352.1,0) rot=(0,0,1;0rad)
  shape: bbox 1750 x 450 x 2e-07 mm, 3 faces, 0 solids (baked)
FEATURE [Part::Feature] mirror320  label="Mirror of Mirror of Mirror of Sofa - 026"
  Placement = pos=(24046.8,-19352.1,0) rot=(0,0,1;0rad)
  shape: bbox 750 x 1883 x 2e-07 mm, 2 faces, 0 solids (baked)
FEATURE [Part::Feature] mirror321  label="Mirror of Mirror of Rectangle208"
  Placement = pos=(24046.8,-19352.1,0) rot=(0,0,1;0rad)
  shape: bbox 950 x 950 x 2e-07 mm, 1 faces, 0 solids (baked)
FEATURE [Part::Feature] mirror322  label="Mirror of Mirror of Sofa - 027"
  Placement = pos=(24046.8,-19352.1,0) rot=(0,0,1;0rad)
  shape: bbox 1883 x 750 x 2e-07 mm, 2 faces, 0 solids (baked)
FEATURE [Part::Part2DObjectPython] Rectangle208  # Draft 2D object (typed FeaturePython)
  ChamferSize = 0
  Columns = 1
  FilletRadius = 0
  Height = 152.175
  Length = 1352.17
  MakeFace = true
  Placement = pos=(46066.7,-15011.1,0) rot=(0,0,1;1.5708rad)
  Rows = 1
FEATURE [Part::Part2DObjectPython] Rectangle209  # Draft 2D object (typed FeaturePython)
  ChamferSize = 0
  Columns = 1
  FilletRadius = 0
  Height = 3000.87
  Length = 6589.69
  MakeFace = true
  Placement = pos=(30046.5,-8675.04,0) rot=(0,0,-1;1.5708rad)
  Rows = 1
FEATURE [Part::Part2DObjectPython] Rectangle210  # Draft 2D object (typed FeaturePython)
  ChamferSize = 0
  Columns = 1
  FilletRadius = 0
  Height = 152.174
  Length = 1748.6
  MakeFace = true
  Placement = pos=(44319.5,-13658.9,0) rot=(0,0,1;0rad)
  Rows = 1
FEATURE [Part::Part2DObjectPython] Rectangle211  # Draft 2D object (typed FeaturePython)
  ChamferSize = 0
  Columns = 1
  FilletRadius = 0
  Height = 152.174
  Length = 967.049
  MakeFace = true
  Placement = pos=(44947.5,-15011.1,0) rot=(0,0,1;0rad)
  Rows = 1
FEATURE [Part::Feature] mirror324  label="Mirror of Mirror of 90cm door022"
  Placement = pos=(-18098.2,9646.33,0) rot=(0,0,-1;1.5708rad)
  shape: bbox 972 x 1000 x 2e-07 mm, 5 faces, 0 solids (baked)
FEATURE [Part::Feature] mirror326  label="Mirror of Mirror of DWire023"
  Placement = pos=(16001.4,-19352.1,0) rot=(0,0,1;0rad)
  shape: bbox 1894 x 2542 x 2e-07 mm, 1 faces, 0 solids (baked)
FEATURE [Part::Feature] mirror327  label="Mirror of Mirror of Mirror of Mirror of 90cm door026"
  Placement = pos=(16001.4,-19352.1,0) rot=(0,0,1;0rad)
  shape: bbox 972 x 1000 x 2e-07 mm, 5 faces, 0 solids (baked)
FEATURE [Part::Mirroring] mirror328  label="Mirror of Mirror of Mirror of Rectangle207"
  Base = (35975.8,-20834.6,0)
  Normal = (0,1,0)
FEATURE [Part::Mirroring] mirror329  label="Mirror of Mirror of Mirror of Rectangle206"
  Base = (35975.8,-20834.6,0)
  Normal = (0,1,0)
FEATURE [Part::Mirroring] mirror330  label="Mirror of Mirror of Mirror of Rectangle205"
  Base = (35975.8,-20834.6,0)
  Normal = (0,1,0)
FEATURE [Part::Mirroring] mirror331  label="Mirror of Mirror of Mirror of Mirror of Mirror of Mirror of Rectangle189"
  Base = (35975.8,-20834.6,0)
  Normal = (0,1,0)
FEATURE [Part::Mirroring] mirror332  label="Mirror of Mirror of Mirror of Mirror of Mirror of Mirror of Rectangle190"
  Base = (35975.8,-20834.6,0)
  Normal = (0,1,0)
FEATURE [Part::Mirroring] mirror333  label="Mirror of Bed-Double009"
  Base = (35975.8,-20834.6,0)
  Normal = (0,1,0)
FEATURE [Part::Mirroring] mirror334  label="Mirror of Mirror of 90cm door020"
  Base = (35975.8,-20834.6,0)
  Normal = (0,1,0)
FEATURE [Part::Mirroring] mirror342  label="Mirror of Compound092"
  Base = (43246.2,-9834.65,0)
  Normal = (-1.6e-11,1,0)
  Placement = pos=(15021.2,-253.409,0) rot=(0,0,1;0rad)
FEATURE [Part::Feature] Compound093
  Placement = pos=(25214.6,3017.83,0) rot=(0,0,1.02052;5e-06rad)
  shape: bbox 1894 x 2542 x 2e-07 mm, 6 faces, 0 solids (baked)
FEATURE [Part::Part2DObjectPython] Rectangle215  # Draft 2D object (typed FeaturePython)
  ChamferSize = 0
  Columns = 1
  FilletRadius = 0
  Height = 1749.66
  Length = 1894.44
  MakeFace = true
  Placement = pos=(37464.8,-10891.3,0) rot=(0.707107,0.707107,0;3.14159rad)
  Rows = 1
FEATURE [Part::Feature] mirror379  label="Mirror of Mirror of Mirror of Mirror of Mirror of Rectangle214"
  Placement = pos=(20221,-50812.3,0) rot=(0,0,1;1.5708rad)
  shape: bbox 4000 x 3000 x 2e-07 mm, 1 faces, 0 solids (baked)
FEATURE [Part::Feature] mirror380  label="Mirror of Mirror of Mirror of Mirror of Mirror of Rectangle215"
  Placement = pos=(20221,-50812.3,0) rot=(0,0,1;1.5708rad)
  shape: bbox 4304 x 3304 x 2e-07 mm, 1 faces, 0 solids (baked)
FEATURE [Part::Feature] mirror381  label="Mirror of Mirror of Mirror of Mirror of Mirror of Mirror of Mirror of Mirror of Rectangle195"
  Placement = pos=(20221,-53212.3,0) rot=(0,0,1;1.5708rad)
  shape: bbox 1500 x 600 x 2e-07 mm, 1 faces, 0 solids (baked)
FEATURE [Part::Feature] mirror382  label="Mirror of Mirror of Mirror of Mirror of Mirror of Mirror of Mirror of Mirror of Rectangle196"
  Placement = pos=(20190.8,-51507.8,0) rot=(0,0,1;1.5708rad)
  shape: bbox 603.7 x 603.7 x 2e-07 mm, 1 faces, 0 solids (baked)
FEATURE [Part::Feature] mirror383  label="Mirror of Mirror of Mirror of Mirror of Mirror of Rectangle216"
  Placement = pos=(20221,-53212.3,0) rot=(0,0,1;1.5708rad)
  shape: bbox 2500 x 600 x 2e-07 mm, 1 faces, 0 solids (baked)
FEATURE [Part::Feature] mirror384  label="Mirror of Mirror of Mirror of Bed-Double012"
  Placement = pos=(20221,-50112.3,0) rot=(0,0,1;1.5708rad)
  shape: bbox 1900 x 1400 x 2e-07 mm, 4 faces, 0 solids (baked)
FEATURE [Part::Feature] mirror385  label="Mirror of Compound093"
  Placement = pos=(30461.2,-71174.2,0) rot=(0,0,1;1.5708rad)
  shape: bbox 2542 x 1894 x 2e-07 mm, 6 faces, 0 solids (baked)
FEATURE [Part::Part2DObjectPython] Rectangle217  # Draft 2D object (typed FeaturePython)
  ChamferSize = 0
  Columns = 1
  FilletRadius = 0
  Height = 3152.17
  Length = 152.173
  MakeFace = true
  Placement = pos=(43331,-12411.6,0) rot=(0.707107,0.707107,0;3.14159rad)
  Rows = 1
FEATURE [Part::Part2DObjectPython] Rectangle218  # Draft 2D object (typed FeaturePython)
  ChamferSize = 0
  Columns = 1
  FilletRadius = 0
  Height = 2370.27
  Length = 152.173
  MakeFace = true
  Placement = pos=(40808.5,-12411.6,0) rot=(0.707107,0.707107,0;3.14159rad)
  Rows = 1
FEATURE [Part::Part2DObjectPython] DWire020  # Draft 2D object (typed FeaturePython)
  ChamferSize = 0
  Closed = true
  End = (41511.8,2520.35,0)
  FilletRadius = 0
  Length = 21875.6
  MakeFace = true
  Points = (11) [(40332.4,-1204.3,0),(40332.4,-1050.76,0),(38903.5,-1050.76,0),(38903.5,-2957.85,0),(41457.9,-2957.85,0),(41457.9,-1050.76,0),(41304.4,-1050.76,0),+4 more]
  Start = (40332.4,-1204.3,0)
  Subdivisions = 0
FEATURE [Part::Part2DObjectPython] DWire021  # Draft 2D object (typed FeaturePython)
  ChamferSize = 0
  Closed = true
  End = (27933.9,-16796.3,0)
  FilletRadius = 0
  Length = 14980.7
  MakeFace = true
  Placement = pos=(-11123.2,-15592,0) rot=(0,0,1;0rad)
  Points = (11) [(40332.4,-1204.3,0),(40332.4,-1050.76,0),(38903.5,-1050.76,0),(38903.5,-2957.85,0),(41457.9,-2957.85,0),(41457.9,-1050.76,0),(41304.4,-1050.76,0),+4 more]
  Start = (29209.2,-16796.3,0)
  Subdivisions = 0
FEATURE [Part::Feature] mirror394  label="Mirror of 90cm door023"
  Placement = pos=(25234.7,3073.98,0) rot=(0,0,-1;1.5708rad)
  shape: bbox 972 x 1000 x 2e-07 mm, 5 faces, 0 solids (baked)
FEATURE [Part::Part2DObjectPython] DWire022  # Draft 2D object (typed FeaturePython)
  ChamferSize = 0
  Closed = true
  End = (33047.4,-13663.8,0)
  FilletRadius = 0
  Length = 35087.2
  MakeFace = true
  Points = (8) [(33047.4,-8675.04,0),(30046.5,-8675.04,0),(30046.5,-15264.7,0),(39601.8,-15264.7,0),(39601.8,-12265.1,0),(35601.8,-12265.1,0),(35601.8,-13663.8,0),+1 more]
  Start = (33047.4,-8675.04,0)
  Subdivisions = 0
FEATURE [Part::Part2DObjectPython] Rectangle219  # Draft 2D object (typed FeaturePython)
  ChamferSize = 0
  Columns = 1
  FilletRadius = 0
  Height = 3000
  Length = 3000
  MakeFace = true
  Placement = pos=(42093.4,-10342.2,0) rot=(0.707107,0.707107,0;3.14159rad)
  Rows = 1
FEATURE [Part::Part2DObjectPython] Rectangle220  # Draft 2D object (typed FeaturePython)
  ChamferSize = 0
  Columns = 1
  FilletRadius = 0
  Height = 3000
  Length = 3000
  MakeFace = true
  Placement = pos=(33047.4,-11522.5,0) rot=(0.707107,0.707107,0;3.14159rad)
  Rows = 1
FEATURE [Part::Part2DObjectPython] DWire023  # Draft 2D object (typed FeaturePython)
  ChamferSize = 0
  Closed = true
  End = (41665.5,-10092,0)
  FilletRadius = 0
  Length = 14474.8
  MakeFace = true
  Placement = pos=(6215.93,3418.23,0) rot=(0,0,1;0rad)
  Points = (6) [(35449.6,-12113,0),(34474.9,-12113,0),(34474.9,-8522.46,0),(33200,-8522.47,0),(33200,-13510.2,0),(35449.6,-13510.2,0)]
  Start = (41665.5,-8694.73,0)
  Subdivisions = 0
FEATURE [Part::Mirroring] mirror395  label="Mirror of Rectangle221"
  Base = (34474.9,-10317.7,0)
  Normal = (0,1,0)
  Placement = pos=(6215.93,2020.97,0) rot=(0,0,1;0rad)
FEATURE [Part::Feature] mirror396  label="Mirror of Mirror of 90cm door023"
  Placement = pos=(28858.8,-4832.33,0) rot=(0,0,-1;1.5708rad)
  shape: bbox 972 x 1000 x 2e-07 mm, 5 faces, 0 solids (baked)
FEATURE [Part::Feature] mirror397  label="Mirror of Compound094"
  Placement = pos=(33776.3,-71661.5,0) rot=(0,0,1;1.5708rad)
  shape: bbox 2542 x 1894 x 2e-07 mm, 6 faces, 0 solids (baked)
FEATURE [Part::Feature] mirror411  label="Mirror of Mirror of Mirror of Sofa - 028"
  Placement = pos=(-25458.1,26638.9,0) rot=(0,0,1;0rad)
  shape: bbox 1883 x 750 x 2e-07 mm, 2 faces, 0 solids (baked)
FEATURE [Part::Feature] mirror412  label="Mirror of Mirror of Rectangle209"
  Placement = pos=(-25458.1,26638.9,0) rot=(0,0,1;0rad)
  shape: bbox 603.7 x 603.7 x 2e-07 mm, 1 faces, 0 solids (baked)
FEATURE [Part::Feature] mirror413  label="Mirror of Mirror of Mirror of Rectangle209"
  Placement = pos=(-25458.1,26638.9,0) rot=(0,0,1;0rad)
  shape: bbox 950 x 950 x 2e-07 mm, 1 faces, 0 solids (baked)
FEATURE [Part::Feature] mirror414  label="Mirror of Mirror of Mirror of Mirror of Sofa - 027"
  Placement = pos=(-25458.1,26638.9,0) rot=(0,0,1;0rad)
  shape: bbox 750 x 1883 x 2e-07 mm, 2 faces, 0 solids (baked)
FEATURE [Part::Feature] mirror417  label="Mirror of Mirror of Mirror of Mirror of Array013"
  Placement = pos=(-25458.1,26638.9,0) rot=(0,0,1;0rad)
  shape: bbox 1750 x 450 x 2e-07 mm, 3 faces, 0 solids (baked)
FEATURE [Part::Feature] mirror418  label="Mirror of Mirror of Mirror of Mirror of Rectangle181"
  Placement = pos=(-25458.1,26638.9,0) rot=(0,0,1;0rad)
  shape: bbox 1801 x 800 x 2e-07 mm, 1 faces, 0 solids (baked)
FEATURE [Part::Feature] mirror419  label="Mirror of Rectangle222"
  Placement = pos=(-25458.1,26638.9,0) rot=(0,0,1;0rad)
  shape: bbox 3306 x 6895 x 2e-07 mm, 1 faces, 0 solids (baked)
FEATURE [Part::Feature] mirror420  label="Mirror of Rectangle223"
  Placement = pos=(-25458.1,26638.9,0) rot=(0,0,1;0rad)
  shape: bbox 3001 x 6590 x 2e-07 mm, 1 faces, 0 solids (baked)
FEATURE [Part::Feature] mirror421  label="Mirror of Mirror of Line048"
  Placement = pos=(-25458.1,26638.9,0) rot=(0,0,1;0rad)
  shape: bbox 3001 x 0.0004885 x 2e-07 mm, 0 faces, 0 solids (baked)
FEATURE [Part::Feature] mirror422  label="Mirror of Mirror of Rectangle210"
  Placement = pos=(-25458.1,26638.9,0) rot=(0,0,1;0rad)
  shape: bbox 3001 x 600 x 2e-07 mm, 1 faces, 0 solids (baked)
FEATURE [Part::Feature] mirror423  label="Mirror of Mirror of Mirror of Sink 015"
  Placement = pos=(-25458.1,26638.9,0) rot=(0,0,1;0rad)
  shape: bbox 500 x 300 x 2e-07 mm, 3 faces, 0 solids (baked)
FEATURE [Part::Feature] mirror437  label="Mirror of Mirror of Rectangle224"
  Placement = pos=(-9508.97,412.332,0) rot=(0,0,1;0rad)
  shape: bbox 3306 x 6895 x 2e-07 mm, 1 faces, 0 solids (baked)
FEATURE [Part::Feature] mirror438  label="Mirror of Mirror of Rectangle225"
  Placement = pos=(-25444.8,26187,0) rot=(0,0,1;0rad)
  shape: bbox 3001 x 6590 x 2e-07 mm, 1 faces, 0 solids (baked)
FEATURE [Part::Feature] mirror439  label="Mirror of Mirror of Mirror of Line049"
  Placement = pos=(-25444.8,26187,0) rot=(0,0,1;0rad)
  shape: bbox 3001 x 0.0004885 x 2e-07 mm, 0 faces, 0 solids (baked)
FEATURE [Part::Feature] mirror440  label="Mirror of Mirror of Mirror of Rectangle212"
  Placement = pos=(-25444.8,26187,0) rot=(0,0,1;0rad)
  shape: bbox 3001 x 600 x 2e-07 mm, 1 faces, 0 solids (baked)
FEATURE [Part::Feature] mirror441  label="Mirror of Mirror of Mirror of Mirror of Sink 016"
  Placement = pos=(-25444.8,26187,0) rot=(0,0,1;0rad)
  shape: bbox 500 x 300 x 2e-07 mm, 3 faces, 0 solids (baked)
FEATURE [Part::Feature] mirror442  label="Mirror of Mirror of Mirror of Mirror of Mirror of Rectangle217"
  Placement = pos=(-25444.8,26187,0) rot=(0,0,1;0rad)
  shape: bbox 1801 x 800 x 2e-07 mm, 1 faces, 0 solids (baked)
FEATURE [Part::Feature] mirror443  label="Mirror of Mirror of Mirror of Mirror of Mirror of Array016"
  Placement = pos=(-25444.8,26187,0) rot=(0,0,1;0rad)
  shape: bbox 1750 x 450 x 2e-07 mm, 3 faces, 0 solids (baked)
FEATURE [Part::Feature] Compound094  label="Door-90cm009"
  Placement = pos=(36125.6,6470.4,0) rot=(0,0,1;0rad)
  shape: bbox 972 x 1000 x 2e-07 mm, 5 faces, 0 solids (baked)
FEATURE [Part::Feature] mirror448  label="Mirror of DWire021"
  Placement = pos=(-1770.22,11655.6,0) rot=(0,0,1;0rad)
  shape: bbox 2554 x 1907 x 2e-07 mm, 1 faces, 0 solids (baked)
FEATURE [Part::Part2DObjectPython] DWire024  # Draft 2D object (typed FeaturePython)
  ChamferSize = 0
  Closed = true
  End = (40287.7,7916.26,0)
  FilletRadius = 0
  Length = 6404.88
  MakeFace = true
  Placement = pos=(19752.2,-5935.01,0) rot=(0,0,1;0rad)
  Points = (6) [(21537.9,13851.3,0),(21537.9,14479.3,0),(19935.5,14479.3,0),(19935.5,12879.3,0),(20535.5,12879.3,0),(20535.5,13851.3,0)]
  Start = (41290.1,7916.26,0)
  Subdivisions = 0
FEATURE [Part::Part2DObjectPython] Rectangle222  # Draft 2D object (typed FeaturePython)
  ChamferSize = 0
  Columns = 1
  FilletRadius = 0
  Height = 1602.44
  Length = 153.543
  MakeFace = true
  Placement = pos=(39687.7,8544.26,0) rot=(0.707107,0.707107,0;3.14159rad)
  Rows = 1
FEATURE [Part::Part2DObjectPython] Rectangle223  # Draft 2D object (typed FeaturePython)
  ChamferSize = 0
  Columns = 1
  FilletRadius = 0
  Height = 1602.44
  Length = 153.543
  MakeFace = true
  Placement = pos=(39687.7,6790.71,0) rot=(0.707107,0.707107,0;3.14159rad)
  Rows = 1
FEATURE [Part::Feature] mirror449  label="Mirror of Mirror of Mirror of 90cm door026"
  Placement = pos=(33457.3,2603.1,0) rot=(0,0,1;0rad)
  shape: bbox 1000 x 972 x 2e-07 mm, 5 faces, 0 solids (baked)
FEATURE [Part::Feature] mirror450  label="Mirror of Mirror of Mirror of Mirror of Mirror of Rectangle218"
  Placement = pos=(24311.6,-32991.6,0) rot=(0,0,1;1.5708rad)
  shape: bbox 4304 x 3304 x 2e-07 mm, 1 faces, 0 solids (baked)
FEATURE [Part::Feature] mirror452  label="Mirror of Mirror of Mirror of Mirror of Mirror of Mirror of Mirror of Mirror of Rectangle197"
  Placement = pos=(24311.6,-35391.6,0) rot=(0,0,1;1.5708rad)
  shape: bbox 1500 x 600 x 2e-07 mm, 1 faces, 0 solids (baked)
FEATURE [Part::Feature] mirror453  label="Mirror of Mirror of Mirror of Mirror of Mirror of Mirror of Mirror of Mirror of Rectangle198"
  Placement = pos=(24281.3,-33687.1,0) rot=(0,0,1;1.5708rad)
  shape: bbox 603.7 x 603.7 x 2e-07 mm, 1 faces, 0 solids (baked)
FEATURE [Part::Part2DObjectPython] Rectangle224  # Draft 2D object (typed FeaturePython)
  ChamferSize = 0
  Columns = 1
  FilletRadius = 0
  Height = 3999.6
  Length = 3000
  MakeFace = true
  Placement = pos=(37290.5,1955.53,0) rot=(0.707107,0.707107,0;3.14159rad)
  Rows = 1
FEATURE [Part::Feature] mirror455  label="Mirror of Mirror of Mirror of Mirror of Mirror of Sofa - 029"
  Placement = pos=(-69120.9,42912.8,0) rot=(0,0,1;0rad)
  shape: bbox 750 x 1883 x 2e-07 mm, 2 faces, 0 solids (baked)
FEATURE [Part::Feature] mirror456  label="Mirror of Mirror of Mirror of Rectangle214"
  Placement = pos=(-69120.9,42912.8,0) rot=(0,0,1;0rad)
  shape: bbox 603.7 x 603.7 x 2e-07 mm, 1 faces, 0 solids (baked)
FEATURE [Part::Feature] mirror457  label="Mirror of Mirror of Mirror of Mirror of Sofa - 030"
  Placement = pos=(-69120.9,42912.8,0) rot=(0,0,1;0rad)
  shape: bbox 1883 x 750 x 2e-07 mm, 2 faces, 0 solids (baked)
FEATURE [Part::Feature] mirror458  label="Mirror of Mirror of Mirror of Mirror of Rectangle211"
  Placement = pos=(-69120.9,42912.8,0) rot=(0,0,1;0rad)
  shape: bbox 950 x 950 x 2e-07 mm, 1 faces, 0 solids (baked)
FEATURE [Part::Feature] Compound095  label="Sofa - 017"
  Placement = pos=(39751.6,6617.04,0) rot=(0,0,1;1.5708rad)
  shape: bbox 750 x 1400 x 2e-07 mm, 2 faces, 0 solids (baked)
FEATURE [Part::Part2DObjectPython] Rectangle225  # Draft 2D object (typed FeaturePython)
  ChamferSize = 0
  Columns = 1
  FilletRadius = 0
  Height = 1500
  Length = 6894.85
  MakeFace = true
  Placement = pos=(44596.2,1802.95,0) rot=(0.707107,0.707107,0;3.14159rad)
  Rows = 1
FEATURE [Part::Part2DObjectPython] Rectangle228  # Draft 2D object (typed FeaturePython)
  ChamferSize = 0
  Columns = 1
  FilletRadius = 0
  Height = 1683.01
  Length = 153.543
  MakeFace = true
  Placement = pos=(38562.2,5107.7,0) rot=(0,1,0;3.14159rad)
  Rows = 1
FEATURE [Part::Part2DObjectPython] Rectangle229  # Draft 2D object (typed FeaturePython)
  ChamferSize = 0
  Columns = 1
  FilletRadius = 0
  Height = 3000.4
  Length = 600.001
  MakeFace = true
  Placement = pos=(40690.1,1955.13,0) rot=(0,0,1;0rad)
  Rows = 1
FEATURE [Part::Feature] mirror464  label="Mirror of Door-90cm013"
  Placement = pos=(-14779.8,23985.9,0) rot=(0,0,1;0rad)
  shape: bbox 972 x 1000 x 2e-07 mm, 5 faces, 0 solids (baked)
FEATURE [Part::Feature] mirror466  label="Mirror of Mirror of Mirror of Mirror of 90cm door028"
  Placement = pos=(-18863.8,23938.1,0) rot=(0,0,1;0rad)
  shape: bbox 1000 x 972 x 2e-07 mm, 5 faces, 0 solids (baked)
FEATURE [Part::Part2DObjectPython] DWire025  # Draft 2D object (typed FeaturePython)
  ChamferSize = 0
  Closed = true
  End = (39718.1,5107.7,0)
  FilletRadius = 0
  Length = 77743.7
  MakeFace = true
  Placement = pos=(-15935.8,25774.6,0) rot=(0,0,1;0rad)
  Points = (34) [(53074.2,-20666.9,0),(53074.2,-23971.3,0),(60532,-23971.3,0),(60532,-17076.8,0),(53069.1,-17076.8,0),(53069.1,-18983.9,0),(54344.4,-18983.9,0),+27 more]
  Start = (37138.4,5107.7,0)
  Subdivisions = 0
FEATURE [Part::Part2DObjectPython] DWire026  # Draft 2D object (typed FeaturePython)
  ChamferSize = 0
  Closed = true
  End = (37286.8,6944.26,0)
  FilletRadius = 0
  Length = 30034.2
  MakeFace = true
  Placement = pos=(-15935.8,25774.6,0) rot=(0,0,1;0rad)
  Points = (8) [(53222.6,-17230.4,0),(60379.4,-17230.4,0),(60379.4,-23819.1,0),(53226.3,-23819.1,0),(53226.3,-20819.1,0),(54498,-20819.1,0),(54498,-18830.4,0),+1 more]
  Start = (37286.8,8544.26,0)
  Subdivisions = 0
FEATURE [Part::Feature] mirror467  label="Mirror of 90cm door024"
  Placement = pos=(11729.4,-2206.29,0) rot=(0,0,1;0rad)
  shape: bbox 1000 x 972 x 2e-07 mm, 5 faces, 0 solids (baked)
FEATURE [Part::Feature] mirror468  label="Mirror of Mirror of Mirror of Mirror of 90cm door029"
  Placement = pos=(11729.4,-2206.29,0) rot=(0,0,1;0rad)
  shape: bbox 1000 x 972 x 2e-07 mm, 5 faces, 0 solids (baked)
FEATURE [Part::Feature] mirror469  label="Mirror of 90cm door025"
  Placement = pos=(11729.4,1235.31,0) rot=(0,0,1;0rad)
  shape: bbox 1000 x 972 x 2e-07 mm, 5 faces, 0 solids (baked)
FEATURE [Part::Feature] mirror470  label="Mirror of WC006"
  Placement = pos=(47128.3,9095.29,0) rot=(0,0,-1;1.5708rad)
  shape: bbox 660 x 370 x 2e-07 mm, 2 faces, 0 solids (baked)
FEATURE [Part::Feature] mirror471  label="Mirror of Sink 013"
  Placement = pos=(47128.3,9171.4,0) rot=(0,0,-1;1.5708rad)
  shape: bbox 500 x 300 x 2e-07 mm, 3 faces, 0 solids (baked)
FEATURE [Part::Feature] mirror472  label="Mirror of Shower006"
  Placement = pos=(47128.3,9021.4,0) rot=(0,0,-1;1.5708rad)
  shape: bbox 800 x 800 x 2e-07 mm, 2 faces, 0 solids (baked)
FEATURE [Part::Part2DObjectPython] Rectangle230  # Draft 2D object (typed FeaturePython)
  ChamferSize = 0
  Columns = 1
  FilletRadius = 0
  Height = 2554.41
  Length = 1907.09
  MakeFace = false
  Placement = pos=(45460.2,-9909.04,0) rot=(0,0,-1;1.5708rad)
  Rows = 1
FEATURE [Part::Part2DObjectPython] Rectangle231  # Draft 2D object (typed FeaturePython)
  ChamferSize = 0
  Columns = 1
  FilletRadius = 0
  Height = 2247.32
  Length = 1600
  MakeFace = false
  Placement = pos=(45613.7,-10062.6,0) rot=(0,0,-1;1.5708rad)
  Rows = 1
  Support = -> [Compound030]
FEATURE [Part::Feature] mirror473  label="Mirror of Mirror of WC011"
  Placement = pos=(14060.3,-12866.9,0) rot=(0,0,1;0rad)
  shape: bbox 660 x 370 x 2e-07 mm, 2 faces, 0 solids (baked)
FEATURE [Part::Feature] mirror474  label="Mirror of Mirror of Sink 015"
  Placement = pos=(14060.3,-12866.9,0) rot=(0,0,1;0rad)
  shape: bbox 500 x 300 x 2e-07 mm, 3 faces, 0 solids (baked)
FEATURE [Part::Feature] mirror475  label="Mirror of Mirror of Shower010"
  Placement = pos=(14060.3,-12866.9,0) rot=(0,0,1;0rad)
  shape: bbox 800 x 800 x 2e-07 mm, 2 faces, 0 solids (baked)
FEATURE [Part::Feature] mirror476  label="Mirror of Rectangle224"
  Placement = pos=(14060.3,-12866.9,0) rot=(0,0,1;0rad)
  shape: bbox 2554 x 1907 x 2e-07 mm, 0 faces, 0 solids (baked)
FEATURE [Part::Feature] mirror477  label="Mirror of Rectangle225"
  Placement = pos=(14060.3,-12866.9,0) rot=(0,0,1;0rad)
  shape: bbox 2247 x 1600 x 2e-07 mm, 0 faces, 0 solids (baked)
FEATURE [Part::Feature] mirror478  label="Mirror of 90cm door026"
  Placement = pos=(46666.3,9880.71,0) rot=(0,0,-1;1.5708rad)
  shape: bbox 972 x 1000 x 2e-07 mm, 5 faces, 0 solids (baked)
FEATURE [Part::Feature] mirror479  label="Mirror of Mirror of Mirror of Rectangle215"
  Placement = pos=(11396.2,10325.4,0) rot=(0,0,1;0rad)
  shape: bbox 950 x 950 x 2e-07 mm, 1 faces, 0 solids (baked)
FEATURE [Part::Feature] mirror480  label="Mirror of Mirror of Mirror of Sofa - 029"
  Placement = pos=(11396.2,10325.4,0) rot=(0,0,1;0rad)
  shape: bbox 1883 x 750 x 2e-07 mm, 2 faces, 0 solids (baked)
FEATURE [Part::Feature] mirror481  label="Mirror of Mirror of Rectangle226"
  Placement = pos=(11396.2,10325.4,0) rot=(0,0,1;0rad)
  shape: bbox 603.7 x 603.7 x 2e-07 mm, 1 faces, 0 solids (baked)
FEATURE [Part::Feature] mirror454  label="Mirror of Mirror of Mirror of Bed-Double013"
  Placement = pos=(3493.37,18934.5,0) rot=(0,0,1;0rad)
  shape: bbox 1400 x 1900 x 2e-07 mm, 4 faces, 0 solids (baked)
FEATURE [Part::Feature] mirror482  label="Mirror of WC007"
  Placement = pos=(38801.4,27702.1,0) rot=(0,0,-1;1.5708rad)
  shape: bbox 660 x 370 x 2e-07 mm, 2 faces, 0 solids (baked)
FEATURE [Part::Feature] mirror483  label="Mirror of Shower007"
  Placement = pos=(38801.4,27628.2,0) rot=(0,0,-1;1.5708rad)
  shape: bbox 800 x 800 x 2e-07 mm, 2 faces, 0 solids (baked)
FEATURE [Part::Feature] mirror484  label="Mirror of Sink 014"
  Placement = pos=(38801.4,27778.2,0) rot=(0,0,-1;1.5708rad)
  shape: bbox 500 x 300 x 2e-07 mm, 3 faces, 0 solids (baked)
FEATURE [App::DocumentObjectGroup] Group008  label="Plan 1"
  Group = -> [Rectangle150,mirror136,mirror137,mirror138,Compound075,Rectangle151,Line037,Line039,Compound076,Line040,Rectangle152,Rectangle153,Array,DWire008,DWire009,Compound077,Rectangle157,Rectangle158,Rectangle161,Rectangle163,Rectangle166,Rectangle167,Clone002,Compound078,mirror139,Rectangle168,Rectangle169,DWire010,DWire011,mirror145,mirror146,mirror147,mirror148,DWire012,mirror200,mirror201,+3 more]
FEATURE [App::DocumentObjectGroup] Group009  label="Plan 2"
  Group = -> [mirror439,mirror440,mirror441,mirror442,mirror443,Compound094,DWire024,mirror449,mirror450,mirror452,mirror453,Rectangle224,Compound095,Rectangle225,Rectangle229,mirror464,mirror466,DWire025,DWire026,mirror467,mirror468,mirror469,mirror479,mirror480,mirror481,mirror454,mirror482,mirror483,mirror484]
FEATURE [App::DocumentObjectGroup] Group010  label="All Other"
  Group = -> [Rectangle016,Rectangle022,Rectangle023,Rectangle024,Face,Rectangle025,Line001,Line002,Block,Rectangle026,Circle,Compound003,Rectangle027,Face004,Compound004,Group003,Rectangle028,mirror008,Construction,Compound021,Compound011,Compound022,Compound008,mirror009,Shell003,mirror013,Compound034,Rectangle072,mirror030,Compound048,Compound049,Line016,Rectangle078,Line017,Compound,Rectangle082,Group007,+198 more]
FEATURE [App::DocumentObjectGroup] Group011  label="Assets001"
  Group = -> [Line048,Rectangle195,Rectangle194,Rectangle193,mirror218,mirror219,mirror220,Rectangle196,Compound087,Rectangle197,Compound089,mirror326,mirror327]
